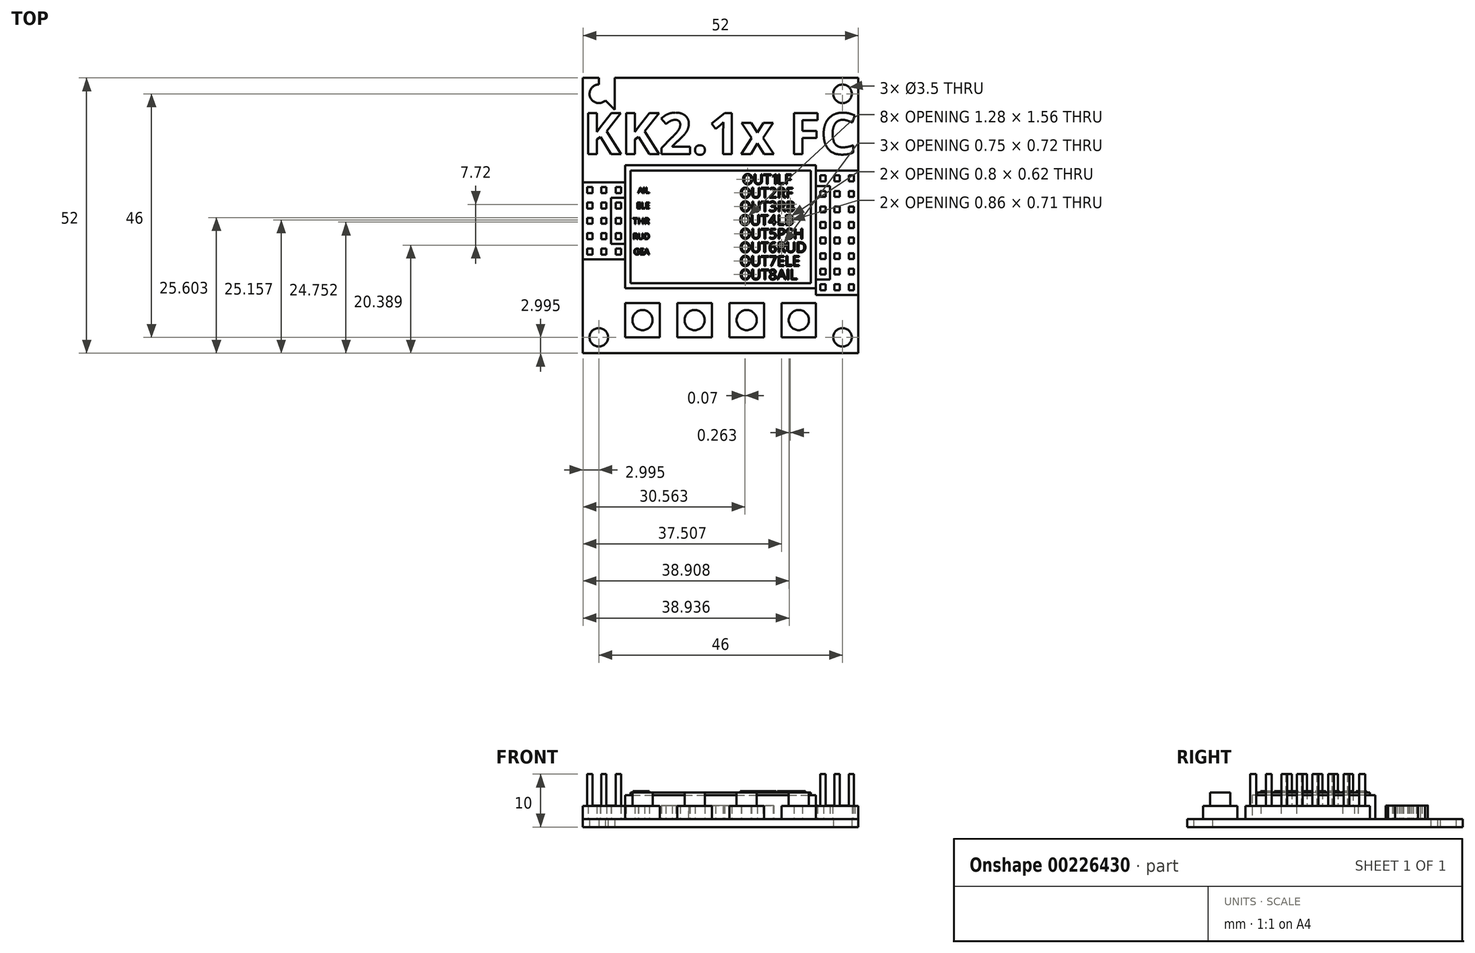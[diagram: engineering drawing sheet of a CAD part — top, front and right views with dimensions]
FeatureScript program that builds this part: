
annotation { "Feature Type Name" : "Feature", "Feature Type Description" : "" }
export const myFeature = defineFeature(function(context is Context, id is Id, definition is map)
    precondition{}
    {
        {
            var Q0;
            Q0=qCreatedBy(makeId("Top.planeOp"),FACE);
            var sketch = newSketch(context, id + "F0", { "sketchPlane" : qUnion([Q0])});
            skLineSegment(sketch, "E0.bottom", {"start": v(-23.53, 22.59) * mm, "end": v(28.47, 22.59) * mm});
            skLineSegment(sketch, "E0.top", {"start": v(-23.53, -29.41) * mm, "end": v(28.47, -29.41) * mm});
            skLineSegment(sketch, "E0.left", {"start": v(-23.53, 22.59) * mm, "end": v(-23.53, -29.41) * mm});
            skLineSegment(sketch, "E0.right", {"start": v(28.47, 22.59) * mm, "end": v(28.47, -29.41) * mm});
            skLineSegment(sketch, "E1", {"start": v(-23.53, 16.59) * mm, "end": v(28.47, 16.59) * mm});
            skLineSegment(sketch, "E2", {"start": v(28.47, -23.41) * mm, "end": v(-23.53, -23.41) * mm});
            skLineSegment(sketch, "E3", {"start": v(-17.53, -29.41) * mm, "end": v(-17.53, 22.59) * mm});
            skLineSegment(sketch, "E4", {"start": v(22.47, 22.59) * mm, "end": v(22.47, -29.41) * mm});
            skLineSegment(sketch, "E5", {"start": v(-23.53, 22.59) * mm, "end": v(-17.53, 16.59) * mm});
            skLineSegment(sketch, "E6", {"start": v(-17.53, 22.59) * mm, "end": v(-23.53, 16.59) * mm});
            skLineSegment(sketch, "E7", {"start": v(-17.53, -23.41) * mm, "end": v(-23.53, -29.41) * mm});
            skLineSegment(sketch, "E8", {"start": v(-23.53, -23.41) * mm, "end": v(-17.53, -29.41) * mm});
            skLineSegment(sketch, "E9", {"start": v(22.47, -29.41) * mm, "end": v(28.47, -23.41) * mm});
            skLineSegment(sketch, "E10", {"start": v(28.47, -29.41) * mm, "end": v(22.47, -23.41) * mm});
            skLineSegment(sketch, "E11", {"start": v(22.47, 16.59) * mm, "end": v(28.47, 22.59) * mm});
            skLineSegment(sketch, "E12", {"start": v(22.47, 22.59) * mm, "end": v(28.47, 16.59) * mm});
            skLineSegment(sketch, "E13", {"start": v(-20.53, 19.59) * mm, "end": v(-23.53, 19.59) * mm});
            skCircle(sketch, "E14", {"center": v(-20.53, 19.59) * mm, "radius": 1.75 * mm});
            skCircle(sketch, "E15", {"center": v(25.47, 19.59) * mm, "radius": 1.75 * mm});
            skCircle(sketch, "E16", {"center": v(25.47, -26.41) * mm, "radius": 1.75 * mm});
            skCircle(sketch, "E17", {"center": v(-20.53, -26.41) * mm, "radius": 1.75 * mm});
            skLineSegment(sketch, "E18", {"start": v(-20.53, 19.59) * mm, "end": v(-20.53, 22.59) * mm});
            skSolve(sketch);
        }
        {
            var Q0;
            {var subQ0=sQuery(id+"F0.wireOp",EDGE,"E1");var subQ1=sQuery(id+"F0.wireOp",EDGE,"E0.right");var subQ2=makeQuery(id+"F0.imprint","INTERSECT",VERTEX,{"derivedFrom":[subQ1,subQ0,sQuery(id+"F0.wireOp",EDGE,"E12")]});Q0=makeQuery(id+"F0.imprint","IMPRINT",FACE,{"disambiguationData":[TD([[makeQuery(id+"F0.imprint","IMPRINT",EDGE,{"disambiguationData":[TD([[subQ2,-1.0]])],"derivedFrom":subQ1}),-1.0]])]});}
            var Q1;
            {var subQ0=sQuery(id+"F0.wireOp",EDGE,"E3");var subQ1=sQuery(id+"F0.wireOp",EDGE,"E1");var subQ2=makeQuery(id+"F0.imprint","INTERSECT",VERTEX,{"derivedFrom":[subQ1,subQ0,sQuery(id+"F0.wireOp",EDGE,"E5")]});Q1=makeQuery(id+"F0.imprint","IMPRINT",FACE,{"disambiguationData":[TD([[makeQuery(id+"F0.imprint","IMPRINT",EDGE,{"disambiguationData":[TD([[subQ2,-1.0]])],"derivedFrom":subQ1}),-1.0]])]});}
            var Q2;
            {var subQ0=sQuery(id+"F0.wireOp",EDGE,"E3");var subQ1=sQuery(id+"F0.wireOp",EDGE,"E0.top");var subQ2=makeQuery(id+"F0.imprint","INTERSECT",VERTEX,{"derivedFrom":[subQ1,subQ0,sQuery(id+"F0.wireOp",EDGE,"E8")]});Q2=makeQuery(id+"F0.imprint","IMPRINT",FACE,{"disambiguationData":[TD([[makeQuery(id+"F0.imprint","IMPRINT",EDGE,{"disambiguationData":[TD([[subQ2,-1.0]])],"derivedFrom":subQ1}),1.0]])]});}
            var Q3;
            {var subQ0=sQuery(id+"F0.wireOp",EDGE,"E1");var subQ1=sQuery(id+"F0.wireOp",EDGE,"E0.left");var subQ2=makeQuery(id+"F0.imprint","INTERSECT",VERTEX,{"derivedFrom":[subQ1,subQ0,sQuery(id+"F0.wireOp",EDGE,"E6")]});Q3=makeQuery(id+"F0.imprint","IMPRINT",FACE,{"disambiguationData":[TD([[makeQuery(id+"F0.imprint","IMPRINT",EDGE,{"disambiguationData":[TD([[subQ2,-1.0]])],"derivedFrom":subQ1}),1.0]])]});}
            var Q4;
            {var subQ0=sQuery(id+"F0.wireOp",EDGE,"E3");var subQ1=sQuery(id+"F0.wireOp",EDGE,"E0.bottom");var subQ2=makeQuery(id+"F0.imprint","INTERSECT",VERTEX,{"derivedFrom":[subQ1,subQ0,sQuery(id+"F0.wireOp",EDGE,"E6")]});Q4=makeQuery(id+"F0.imprint","IMPRINT",FACE,{"disambiguationData":[TD([[makeQuery(id+"F0.imprint","IMPRINT",EDGE,{"disambiguationData":[TD([[subQ2,-1.0]])],"derivedFrom":subQ1}),-1.0]])]});}
            var Q5;
            {var subQ3=sQuery(id+"F0.wireOp",EDGE,"E11");var subQ5=sQuery(id+"F0.wireOp",EDGE,"E15");var subQ6=makeQuery(id+"F0.imprint","INTERSECT",VERTEX,{"disambiguationData":[OD(0.0)],"derivedFrom":[subQ3,subQ5]});Q5=makeQuery(id+"F0.imprint","IMPRINT",FACE,{"disambiguationData":[TD([[makeQuery(id+"F0.imprint","IMPRINT",EDGE,{"disambiguationData":[TD([[subQ6,-1.0]])],"derivedFrom":subQ5}),-1.0]])]});}
            var Q6;
            {var subQ0=sQuery(id+"F0.wireOp",EDGE,"E11");var subQ5=sQuery(id+"F0.wireOp",EDGE,"E15");var subQ6=makeQuery(id+"F0.imprint","INTERSECT",VERTEX,{"disambiguationData":[OD(1.0)],"derivedFrom":[subQ0,subQ5]});Q6=makeQuery(id+"F0.imprint","IMPRINT",FACE,{"disambiguationData":[TD([[makeQuery(id+"F0.imprint","IMPRINT",EDGE,{"disambiguationData":[TD([[subQ6,1.0]])],"derivedFrom":subQ5}),-1.0]])]});}
            var Q7;
            {var subQ0=sQuery(id+"F0.wireOp",EDGE,"E11");var subQ5=sQuery(id+"F0.wireOp",EDGE,"E15");var subQ6=makeQuery(id+"F0.imprint","INTERSECT",VERTEX,{"disambiguationData":[OD(1.0)],"derivedFrom":[subQ0,subQ5]});Q7=makeQuery(id+"F0.imprint","IMPRINT",FACE,{"disambiguationData":[TD([[makeQuery(id+"F0.imprint","IMPRINT",EDGE,{"disambiguationData":[TD([[subQ6,-1.0]])],"derivedFrom":subQ5}),-1.0]])]});}
            var Q8;
            {var subQ3=sQuery(id+"F0.wireOp",EDGE,"E11");var subQ5=sQuery(id+"F0.wireOp",EDGE,"E15");var subQ6=makeQuery(id+"F0.imprint","INTERSECT",VERTEX,{"disambiguationData":[OD(0.0)],"derivedFrom":[subQ3,subQ5]});Q8=makeQuery(id+"F0.imprint","IMPRINT",FACE,{"disambiguationData":[TD([[makeQuery(id+"F0.imprint","IMPRINT",EDGE,{"disambiguationData":[TD([[subQ6,1.0]])],"derivedFrom":subQ5}),-1.0]])]});}
            var Q9;
            {var subQ3=sQuery(id+"F0.wireOp",EDGE,"E9");var subQ5=sQuery(id+"F0.wireOp",EDGE,"E16");var subQ6=makeQuery(id+"F0.imprint","INTERSECT",VERTEX,{"disambiguationData":[OD(1.0)],"derivedFrom":[subQ3,subQ5]});Q9=makeQuery(id+"F0.imprint","IMPRINT",FACE,{"disambiguationData":[TD([[makeQuery(id+"F0.imprint","IMPRINT",EDGE,{"disambiguationData":[TD([[subQ6,1.0]])],"derivedFrom":subQ5}),-1.0]])]});}
            var Q10;
            {var subQ0=sQuery(id+"F0.wireOp",EDGE,"E9");var subQ5=sQuery(id+"F0.wireOp",EDGE,"E16");var subQ6=makeQuery(id+"F0.imprint","INTERSECT",VERTEX,{"disambiguationData":[OD(1.0)],"derivedFrom":[subQ0,subQ5]});Q10=makeQuery(id+"F0.imprint","IMPRINT",FACE,{"disambiguationData":[TD([[makeQuery(id+"F0.imprint","IMPRINT",EDGE,{"disambiguationData":[TD([[subQ6,-1.0]])],"derivedFrom":subQ5}),-1.0]])]});}
            var Q11;
            {var subQ0=sQuery(id+"F0.wireOp",EDGE,"E9");var subQ5=sQuery(id+"F0.wireOp",EDGE,"E16");var subQ6=makeQuery(id+"F0.imprint","INTERSECT",VERTEX,{"disambiguationData":[OD(0.0)],"derivedFrom":[subQ0,subQ5]});Q11=makeQuery(id+"F0.imprint","IMPRINT",FACE,{"disambiguationData":[TD([[makeQuery(id+"F0.imprint","IMPRINT",EDGE,{"disambiguationData":[TD([[subQ6,1.0]])],"derivedFrom":subQ5}),-1.0]])]});}
            var Q12;
            {var subQ3=sQuery(id+"F0.wireOp",EDGE,"E9");var subQ5=sQuery(id+"F0.wireOp",EDGE,"E16");var subQ7=makeQuery(id+"F0.imprint","INTERSECT",VERTEX,{"disambiguationData":[OD(0.0)],"derivedFrom":[subQ3,subQ5]});Q12=makeQuery(id+"F0.imprint","IMPRINT",FACE,{"disambiguationData":[TD([[makeQuery(id+"F0.imprint","IMPRINT",EDGE,{"disambiguationData":[TD([[subQ7,-1.0]])],"derivedFrom":subQ5}),-1.0]])]});}
            var Q13;
            {var subQ0=sQuery(id+"F0.wireOp",EDGE,"E7");var subQ5=sQuery(id+"F0.wireOp",EDGE,"E17");var subQ6=makeQuery(id+"F0.imprint","INTERSECT",VERTEX,{"disambiguationData":[OD(1.0)],"derivedFrom":[subQ0,subQ5]});Q13=makeQuery(id+"F0.imprint","IMPRINT",FACE,{"disambiguationData":[TD([[makeQuery(id+"F0.imprint","IMPRINT",EDGE,{"disambiguationData":[TD([[subQ6,-1.0]])],"derivedFrom":subQ5}),-1.0]])]});}
            var Q14;
            {var subQ3=sQuery(id+"F0.wireOp",EDGE,"E7");var subQ5=sQuery(id+"F0.wireOp",EDGE,"E17");var subQ6=makeQuery(id+"F0.imprint","INTERSECT",VERTEX,{"disambiguationData":[OD(0.0)],"derivedFrom":[subQ3,subQ5]});Q14=makeQuery(id+"F0.imprint","IMPRINT",FACE,{"disambiguationData":[TD([[makeQuery(id+"F0.imprint","IMPRINT",EDGE,{"disambiguationData":[TD([[subQ6,1.0]])],"derivedFrom":subQ5}),-1.0]])]});}
            var Q15;
            {var subQ3=sQuery(id+"F0.wireOp",EDGE,"E7");var subQ5=sQuery(id+"F0.wireOp",EDGE,"E17");var subQ6=makeQuery(id+"F0.imprint","INTERSECT",VERTEX,{"disambiguationData":[OD(0.0)],"derivedFrom":[subQ3,subQ5]});Q15=makeQuery(id+"F0.imprint","IMPRINT",FACE,{"disambiguationData":[TD([[makeQuery(id+"F0.imprint","IMPRINT",EDGE,{"disambiguationData":[TD([[subQ6,-1.0]])],"derivedFrom":subQ5}),-1.0]])]});}
            var Q16;
            {var subQ0=sQuery(id+"F0.wireOp",EDGE,"E7");var subQ5=sQuery(id+"F0.wireOp",EDGE,"E17");var subQ6=makeQuery(id+"F0.imprint","INTERSECT",VERTEX,{"disambiguationData":[OD(1.0)],"derivedFrom":[subQ0,subQ5]});Q16=makeQuery(id+"F0.imprint","IMPRINT",FACE,{"disambiguationData":[TD([[makeQuery(id+"F0.imprint","IMPRINT",EDGE,{"disambiguationData":[TD([[subQ6,1.0]])],"derivedFrom":subQ5}),-1.0]])]});}
            var Q17;
            {var subQ1=sQuery(id+"F0.wireOp",EDGE,"E0.left");var subQ3=sQuery(id+"F0.wireOp",EDGE,"E13");var subQ4=makeQuery(id+"F0.imprint","INTERSECT",VERTEX,{"derivedFrom":[subQ1,subQ3]});Q17=makeQuery(id+"F0.imprint","IMPRINT",FACE,{"disambiguationData":[TD([[makeQuery(id+"F0.imprint","IMPRINT",EDGE,{"disambiguationData":[TD([[subQ4,1.0]])],"derivedFrom":subQ3}),-1.0]])]});}
            var Q18;
            {var subQ0=sQuery(id+"F0.wireOp",EDGE,"E5");var subQ5=sQuery(id+"F0.wireOp",EDGE,"E14");var subQ6=makeQuery(id+"F0.imprint","INTERSECT",VERTEX,{"disambiguationData":[OD(0.0)],"derivedFrom":[subQ0,subQ5]});Q18=makeQuery(id+"F0.imprint","IMPRINT",FACE,{"disambiguationData":[TD([[makeQuery(id+"F0.imprint","IMPRINT",EDGE,{"disambiguationData":[TD([[subQ6,1.0]])],"derivedFrom":subQ5}),-1.0]])]});}
            var Q19;
            {var subQ0=sQuery(id+"F0.wireOp",EDGE,"E6");var subQ5=sQuery(id+"F0.wireOp",EDGE,"E14");var subQ6=makeQuery(id+"F0.imprint","INTERSECT",VERTEX,{"disambiguationData":[OD(0.0)],"derivedFrom":[subQ0,subQ5]});Q19=makeQuery(id+"F0.imprint","IMPRINT",FACE,{"disambiguationData":[TD([[makeQuery(id+"F0.imprint","IMPRINT",EDGE,{"disambiguationData":[TD([[subQ6,-1.0]])],"derivedFrom":subQ5}),-1.0]])]});}
            var Q20;
            {var subQ3=sQuery(id+"F0.wireOp",EDGE,"E5");var subQ5=sQuery(id+"F0.wireOp",EDGE,"E14");var subQ6=makeQuery(id+"F0.imprint","INTERSECT",VERTEX,{"disambiguationData":[OD(1.0)],"derivedFrom":[subQ3,subQ5]});Q20=makeQuery(id+"F0.imprint","IMPRINT",FACE,{"disambiguationData":[TD([[makeQuery(id+"F0.imprint","IMPRINT",EDGE,{"disambiguationData":[TD([[subQ6,-1.0]])],"derivedFrom":subQ5}),-1.0]])]});}
            var Q21;
            {var subQ3=sQuery(id+"F0.wireOp",EDGE,"E5");var subQ5=sQuery(id+"F0.wireOp",EDGE,"E14");var subQ6=makeQuery(id+"F0.imprint","INTERSECT",VERTEX,{"disambiguationData":[OD(1.0)],"derivedFrom":[subQ3,subQ5]});Q21=makeQuery(id+"F0.imprint","IMPRINT",FACE,{"disambiguationData":[TD([[makeQuery(id+"F0.imprint","IMPRINT",EDGE,{"disambiguationData":[TD([[subQ6,1.0]])],"derivedFrom":subQ5}),-1.0]])]});}
            var Q22;
            {var subQ1=sQuery(id+"F0.wireOp",EDGE,"E0.left");var subQ3=sQuery(id+"F0.wireOp",EDGE,"E13");var subQ4=makeQuery(id+"F0.imprint","INTERSECT",VERTEX,{"derivedFrom":[subQ1,subQ3]});Q22=makeQuery(id+"F0.imprint","IMPRINT",FACE,{"disambiguationData":[TD([[makeQuery(id+"F0.imprint","IMPRINT",EDGE,{"disambiguationData":[TD([[subQ4,1.0]])],"derivedFrom":subQ3}),1.0]])]});}
            extrude(context, id + "F1", {"entities" : qUnion([Q0, Q1, Q2, Q3, Q4, Q5, Q6, Q7, Q8, Q9, Q10, Q11, Q12, Q13, Q14, Q15, Q16, Q17, Q18, Q19, Q20, Q21, Q22]), "depth" : 1.5 * mm, "offsetDistance" : 25.4 * mm});
        }
        {
            var Q0;
            Q0=makeQuery(id+"F1.opExtrude","CAP_FACE",FACE,{"disambiguationData":[OSD([sQuery(id+"F0.wireOp",EDGE,"E0.bottom"),sQuery(id+"F0.wireOp",EDGE,"E0.top"),sQuery(id+"F0.wireOp",EDGE,"E0.left"),sQuery(id+"F0.wireOp",EDGE,"E0.right"),sQuery(id+"F0.wireOp",EDGE,"E14"),sQuery(id+"F0.wireOp",EDGE,"E15"),sQuery(id+"F0.wireOp",EDGE,"E16"),sQuery(id+"F0.wireOp",EDGE,"E17")])],"isStart":false});
            var sketch = newSketch(context, id + "F2", { "sketchPlane" : qUnion([Q0])});
            skLineSegment(sketch, "E19.bottom", {"start": v(-15.53, 6.09) * mm, "end": v(20.47, 6.09) * mm});
            skLineSegment(sketch, "E19.top", {"start": v(-15.53, -17.16) * mm, "end": v(20.47, -17.16) * mm});
            skLineSegment(sketch, "E19.left", {"start": v(-15.53, 6.09) * mm, "end": v(-15.53, -17.16) * mm});
            skLineSegment(sketch, "E19.right", {"start": v(20.47, 6.09) * mm, "end": v(20.47, -17.16) * mm});
            skLineSegment(sketch, "E20", {"start": v(-15.53, 6.09) * mm, "end": v(-23.53, 6.09) * mm});
            skLineSegment(sketch, "E21", {"start": v(20.47, 6.09) * mm, "end": v(28.47, 6.09) * mm});
            skSolve(sketch);
        }
        {
            var Q0;
            Q0=makeQuery(id+"F2.imprint","IMPRINT",FACE,{"disambiguationData":[TD([[makeQuery(id+"F2.imprint","IMPRINT",EDGE,{"derivedFrom":sQuery(id+"F2.wireOp",EDGE,"E19.bottom")}),-1.0]])]});
            extrude(context, id + "F3", {"entities" : qUnion([Q0]), "depth" : 4.5 * mm, "offsetDistance" : 25.4 * mm});
        }
        {
            var Q0;
            Q0=makeQuery(id+"F3.opExtrude","CAP_FACE",FACE,{"disambiguationData":[OSD([sQuery(id+"F2.wireOp",EDGE,"E19.bottom"),sQuery(id+"F2.wireOp",EDGE,"E19.top"),sQuery(id+"F2.wireOp",EDGE,"E19.left"),sQuery(id+"F2.wireOp",EDGE,"E19.right")])],"isStart":false});
            var sketch = newSketch(context, id + "F4", { "sketchPlane" : qUnion([Q0])});
            skLineSegment(sketch, "E22.bottom", {"start": v(-14.53, 5.09) * mm, "end": v(19.47, 5.09) * mm});
            skLineSegment(sketch, "E22.top", {"start": v(-14.53, -16.16) * mm, "end": v(19.47, -16.16) * mm});
            skLineSegment(sketch, "E22.left", {"start": v(-14.53, 5.09) * mm, "end": v(-14.53, -16.16) * mm});
            skLineSegment(sketch, "E22.right", {"start": v(19.47, 5.09) * mm, "end": v(19.47, -16.16) * mm});
            skLineSegment(sketch, "E23", {"start": v(-14.53, 5.09) * mm, "end": v(-14.53, 6.09) * mm});
            skLineSegment(sketch, "E24", {"start": v(-14.53, -16.16) * mm, "end": v(-14.53, -17.16) * mm});
            skLineSegment(sketch, "E25", {"start": v(19.47, 5.09) * mm, "end": v(20.47, 5.09) * mm});
            skLineSegment(sketch, "E26", {"start": v(-14.53, 5.09) * mm, "end": v(-15.53, 5.09) * mm});
            skSolve(sketch);
        }
        {
            var Q0;
            Q0=makeQuery(id+"F4.imprint","IMPRINT",FACE,{"disambiguationData":[TD([[makeQuery(id+"F4.imprint","IMPRINT",EDGE,{"derivedFrom":sQuery(id+"F4.wireOp",EDGE,"E22.bottom")}),-1.0]])]});
            extrude(context, id + "F5", {"entities" : qUnion([Q0]), "depth" : 0.5 * mm, "offsetDistance" : 25.4 * mm});
        }
        {
            var Q0;
            Q0=makeQuery(id+"F1.opExtrude","CAP_FACE",FACE,{"disambiguationData":[OSD([sQuery(id+"F0.wireOp",EDGE,"E0.bottom"),sQuery(id+"F0.wireOp",EDGE,"E0.top"),sQuery(id+"F0.wireOp",EDGE,"E0.left"),sQuery(id+"F0.wireOp",EDGE,"E0.right"),sQuery(id+"F0.wireOp",EDGE,"E14"),sQuery(id+"F0.wireOp",EDGE,"E15"),sQuery(id+"F0.wireOp",EDGE,"E16"),sQuery(id+"F0.wireOp",EDGE,"E17")])],"isStart":false});
            var sketch = newSketch(context, id + "F6", { "sketchPlane" : qUnion([Q0])});
            skLineSegment(sketch, "E27.0", {"start": v(-15.53, 6.09) * mm, "end": v(-15.53, -17.16) * mm});
            skLineSegment(sketch, "E27.1", {"start": v(-15.53, -17.16) * mm, "end": v(20.47, -17.16) * mm});
            skLineSegment(sketch, "E27.2", {"start": v(20.47, 6.09) * mm, "end": v(20.47, -17.16) * mm});
            skLineSegment(sketch, "E27.3", {"start": v(-15.53, 6.09) * mm, "end": v(20.47, 6.09) * mm});
            skLineSegment(sketch, "E28.bottom", {"start": v(-23.53, 2.84) * mm, "end": v(-15.53, 2.84) * mm});
            skLineSegment(sketch, "E28.top", {"start": v(-23.53, -11.66) * mm, "end": v(-15.53, -11.66) * mm});
            skLineSegment(sketch, "E28.left", {"start": v(-23.53, 2.84) * mm, "end": v(-23.53, -11.66) * mm});
            skLineSegment(sketch, "E28.right", {"start": v(-15.53, 2.84) * mm, "end": v(-15.53, -11.66) * mm});
            skLineSegment(sketch, "E29.bottom", {"start": v(28.47, 5.09) * mm, "end": v(20.47, 5.09) * mm});
            skLineSegment(sketch, "E29.top", {"start": v(28.47, -18.41) * mm, "end": v(20.47, -18.41) * mm});
            skLineSegment(sketch, "E29.left", {"start": v(28.47, 5.09) * mm, "end": v(28.47, -18.41) * mm});
            skLineSegment(sketch, "E29.right", {"start": v(20.47, 5.09) * mm, "end": v(20.47, -18.41) * mm});
            skLineSegment(sketch, "E30", {"start": v(-23.53, -0.06) * mm, "end": v(-15.53, -0.06) * mm});
            skLineSegment(sketch, "E31", {"start": v(-23.53, -2.96) * mm, "end": v(-15.53, -2.96) * mm});
            skLineSegment(sketch, "E32", {"start": v(-23.53, -5.86) * mm, "end": v(-15.53, -5.86) * mm});
            skLineSegment(sketch, "E33", {"start": v(-23.53, -8.76) * mm, "end": v(-15.53, -8.76) * mm});
            skLineSegment(sketch, "E34", {"start": v(-20.91, 2.84) * mm, "end": v(-20.91, -11.66) * mm});
            skLineSegment(sketch, "E35", {"start": v(-18.22, -11.66) * mm, "end": v(-18.22, 2.84) * mm});
            skLineSegment(sketch, "E36", {"start": v(-18.22, 0) * mm, "end": v(-15.53, 2.84) * mm, "construction": true});
            skLineSegment(sketch, "E37", {"start": v(-20.91, 0) * mm, "end": v(-18.22, 2.84) * mm, "construction": true});
            skLineSegment(sketch, "E38", {"start": v(-23.53, -0.06) * mm, "end": v(-20.91, 2.84) * mm, "construction": true});
            skLineSegment(sketch, "E39", {"start": v(-23.53, -0.06) * mm, "end": v(-20.91, -2.96) * mm, "construction": true});
            skLineSegment(sketch, "E40", {"start": v(-20.91, -2.96) * mm, "end": v(-23.53, -5.86) * mm, "construction": true});
            skLineSegment(sketch, "E41", {"start": v(-20.91, -8.76) * mm, "end": v(-23.53, -5.86) * mm, "construction": true});
            skLineSegment(sketch, "E42", {"start": v(-20.91, -8.76) * mm, "end": v(-23.53, -11.66) * mm, "construction": true});
            skLineSegment(sketch, "E43", {"start": v(20.47, -0.79) * mm, "end": v(28.47, -0.79) * mm});
            skLineSegment(sketch, "E44", {"start": v(20.47, -3.73) * mm, "end": v(28.47, -3.73) * mm});
            skLineSegment(sketch, "E45", {"start": v(20.47, -6.66) * mm, "end": v(28.47, -6.66) * mm});
            skLineSegment(sketch, "E46", {"start": v(20.47, -9.6) * mm, "end": v(28.47, -9.6) * mm});
            skLineSegment(sketch, "E47", {"start": v(20.47, -12.54) * mm, "end": v(28.47, -12.54) * mm});
            skLineSegment(sketch, "E48", {"start": v(20.47, -15.48) * mm, "end": v(28.47, -15.48) * mm});
            skLineSegment(sketch, "E49", {"start": v(20.47, 2.15) * mm, "end": v(28.47, 2.15) * mm});
            skLineSegment(sketch, "E50", {"start": v(23.13, 5.09) * mm, "end": v(23.13, -18.41) * mm});
            skLineSegment(sketch, "E51", {"start": v(25.8, -18.41) * mm, "end": v(25.8, 5.09) * mm});
            skLineSegment(sketch, "E52", {"start": v(20.47, 5.09) * mm, "end": v(23.13, 2.15) * mm, "construction": true});
            skLineSegment(sketch, "E53", {"start": v(23.13, 2.15) * mm, "end": v(25.8, 5.09) * mm, "construction": true});
            skLineSegment(sketch, "E54", {"start": v(25.8, 5.09) * mm, "end": v(28.47, 2.15) * mm, "construction": true});
            skLineSegment(sketch, "E55", {"start": v(23.13, 2.15) * mm, "end": v(20.47, -0.79) * mm, "construction": true});
            skLineSegment(sketch, "E56", {"start": v(20.47, -0.79) * mm, "end": v(23.13, -3.73) * mm, "construction": true});
            skLineSegment(sketch, "E57", {"start": v(23.13, -3.73) * mm, "end": v(20.47, -6.66) * mm, "construction": true});
            skLineSegment(sketch, "E58", {"start": v(20.47, -6.66) * mm, "end": v(23.13, -9.6) * mm, "construction": true});
            skLineSegment(sketch, "E59", {"start": v(23.13, -9.6) * mm, "end": v(20.47, -12.54) * mm, "construction": true});
            skLineSegment(sketch, "E60", {"start": v(20.47, -12.54) * mm, "end": v(23.13, -15.48) * mm, "construction": true});
            skLineSegment(sketch, "E61", {"start": v(23.13, -15.48) * mm, "end": v(20.47, -18.41) * mm, "construction": true});
            skSolve(sketch);
        }
        {
            var Q0;
            {var subQ0=sQuery(id+"F6.wireOp",EDGE,"E28.left");var subQ5=sQuery(id+"F6.wireOp",EDGE,"E30");var subQ6=makeQuery(id+"F6.imprint","INTERSECT",VERTEX,{"derivedFrom":[subQ0,subQ5]});Q0=makeQuery(id+"F6.imprint","IMPRINT",FACE,{"disambiguationData":[TD([[makeQuery(id+"F6.imprint","IMPRINT",EDGE,{"disambiguationData":[TD([[subQ6,-1.0]])],"derivedFrom":subQ5}),1.0]])]});}
            var Q1;
            {var subQ0=sQuery(id+"F6.wireOp",EDGE,"E34");var subQ1=sQuery(id+"F6.wireOp",EDGE,"E28.bottom");var subQ2=makeQuery(id+"F6.imprint","INTERSECT",VERTEX,{"derivedFrom":[subQ1,subQ0]});Q1=makeQuery(id+"F6.imprint","IMPRINT",FACE,{"disambiguationData":[TD([[makeQuery(id+"F6.imprint","IMPRINT",EDGE,{"disambiguationData":[TD([[subQ2,-1.0]])],"derivedFrom":subQ1}),-1.0]])]});}
            var Q2;
            {var subQ0=sQuery(id+"F6.wireOp",EDGE,"E28.right");var subQ5=sQuery(id+"F6.wireOp",EDGE,"E30");var subQ7=makeQuery(id+"F6.imprint","INTERSECT",VERTEX,{"derivedFrom":[subQ0,subQ5]});Q2=makeQuery(id+"F6.imprint","IMPRINT",FACE,{"disambiguationData":[TD([[makeQuery(id+"F6.imprint","IMPRINT",EDGE,{"disambiguationData":[TD([[subQ7,1.0]])],"derivedFrom":subQ5}),1.0]])]});}
            var Q3;
            {var subQ0=sQuery(id+"F6.wireOp",EDGE,"E30");var subQ1=sQuery(id+"F6.wireOp",EDGE,"E28.right");var subQ2=makeQuery(id+"F6.imprint","INTERSECT",VERTEX,{"derivedFrom":[subQ1,subQ0]});Q3=makeQuery(id+"F6.imprint","IMPRINT",FACE,{"disambiguationData":[TD([[makeQuery(id+"F6.imprint","IMPRINT",EDGE,{"disambiguationData":[TD([[subQ2,-1.0]])],"derivedFrom":subQ1}),-1.0]])]});}
            var Q4;
            {var subQ0=sQuery(id+"F6.wireOp",EDGE,"E34");var subQ1=sQuery(id+"F6.wireOp",EDGE,"E30");var subQ2=makeQuery(id+"F6.imprint","INTERSECT",VERTEX,{"derivedFrom":[subQ1,subQ0]});Q4=makeQuery(id+"F6.imprint","IMPRINT",FACE,{"disambiguationData":[TD([[makeQuery(id+"F6.imprint","IMPRINT",EDGE,{"disambiguationData":[TD([[subQ2,-1.0]])],"derivedFrom":subQ1}),-1.0]])]});}
            var Q5;
            {var subQ0=sQuery(id+"F6.wireOp",EDGE,"E30");var subQ1=sQuery(id+"F6.wireOp",EDGE,"E28.left");var subQ2=makeQuery(id+"F6.imprint","INTERSECT",VERTEX,{"derivedFrom":[subQ1,subQ0]});Q5=makeQuery(id+"F6.imprint","IMPRINT",FACE,{"disambiguationData":[TD([[makeQuery(id+"F6.imprint","IMPRINT",EDGE,{"disambiguationData":[TD([[subQ2,-1.0]])],"derivedFrom":subQ1}),1.0]])]});}
            var Q6;
            {var subQ0=sQuery(id+"F6.wireOp",EDGE,"E31");var subQ1=sQuery(id+"F6.wireOp",EDGE,"E28.left");var subQ2=makeQuery(id+"F6.imprint","INTERSECT",VERTEX,{"derivedFrom":[subQ1,subQ0]});Q6=makeQuery(id+"F6.imprint","IMPRINT",FACE,{"disambiguationData":[TD([[makeQuery(id+"F6.imprint","IMPRINT",EDGE,{"disambiguationData":[TD([[subQ2,-1.0]])],"derivedFrom":subQ1}),1.0]])]});}
            var Q7;
            {var subQ0=sQuery(id+"F6.wireOp",EDGE,"E34");var subQ1=sQuery(id+"F6.wireOp",EDGE,"E31");var subQ2=makeQuery(id+"F6.imprint","INTERSECT",VERTEX,{"derivedFrom":[subQ1,subQ0]});Q7=makeQuery(id+"F6.imprint","IMPRINT",FACE,{"disambiguationData":[TD([[makeQuery(id+"F6.imprint","IMPRINT",EDGE,{"disambiguationData":[TD([[subQ2,-1.0]])],"derivedFrom":subQ1}),-1.0]])]});}
            var Q8;
            {var subQ0=sQuery(id+"F6.wireOp",EDGE,"E31");var subQ1=sQuery(id+"F6.wireOp",EDGE,"E28.right");var subQ2=makeQuery(id+"F6.imprint","INTERSECT",VERTEX,{"derivedFrom":[subQ1,subQ0]});Q8=makeQuery(id+"F6.imprint","IMPRINT",FACE,{"disambiguationData":[TD([[makeQuery(id+"F6.imprint","IMPRINT",EDGE,{"disambiguationData":[TD([[subQ2,-1.0]])],"derivedFrom":subQ1}),-1.0]])]});}
            var Q9;
            {var subQ0=sQuery(id+"F6.wireOp",EDGE,"E32");var subQ1=sQuery(id+"F6.wireOp",EDGE,"E28.right");var subQ2=makeQuery(id+"F6.imprint","INTERSECT",VERTEX,{"derivedFrom":[subQ1,subQ0]});Q9=makeQuery(id+"F6.imprint","IMPRINT",FACE,{"disambiguationData":[TD([[makeQuery(id+"F6.imprint","IMPRINT",EDGE,{"disambiguationData":[TD([[subQ2,-1.0]])],"derivedFrom":subQ1}),-1.0]])]});}
            var Q10;
            {var subQ0=sQuery(id+"F6.wireOp",EDGE,"E34");var subQ1=sQuery(id+"F6.wireOp",EDGE,"E32");var subQ2=makeQuery(id+"F6.imprint","INTERSECT",VERTEX,{"derivedFrom":[subQ1,subQ0]});Q10=makeQuery(id+"F6.imprint","IMPRINT",FACE,{"disambiguationData":[TD([[makeQuery(id+"F6.imprint","IMPRINT",EDGE,{"disambiguationData":[TD([[subQ2,-1.0]])],"derivedFrom":subQ1}),-1.0]])]});}
            var Q11;
            {var subQ0=sQuery(id+"F6.wireOp",EDGE,"E32");var subQ1=sQuery(id+"F6.wireOp",EDGE,"E28.left");var subQ2=makeQuery(id+"F6.imprint","INTERSECT",VERTEX,{"derivedFrom":[subQ1,subQ0]});Q11=makeQuery(id+"F6.imprint","IMPRINT",FACE,{"disambiguationData":[TD([[makeQuery(id+"F6.imprint","IMPRINT",EDGE,{"disambiguationData":[TD([[subQ2,-1.0]])],"derivedFrom":subQ1}),1.0]])]});}
            var Q12;
            {var subQ0=sQuery(id+"F6.wireOp",EDGE,"E28.left");var subQ5=sQuery(id+"F6.wireOp",EDGE,"E33");var subQ6=makeQuery(id+"F6.imprint","INTERSECT",VERTEX,{"derivedFrom":[subQ0,subQ5]});Q12=makeQuery(id+"F6.imprint","IMPRINT",FACE,{"disambiguationData":[TD([[makeQuery(id+"F6.imprint","IMPRINT",EDGE,{"disambiguationData":[TD([[subQ6,-1.0]])],"derivedFrom":subQ5}),-1.0]])]});}
            var Q13;
            {var subQ0=sQuery(id+"F6.wireOp",EDGE,"E34");var subQ1=sQuery(id+"F6.wireOp",EDGE,"E28.top");var subQ2=makeQuery(id+"F6.imprint","INTERSECT",VERTEX,{"derivedFrom":[subQ1,subQ0]});Q13=makeQuery(id+"F6.imprint","IMPRINT",FACE,{"disambiguationData":[TD([[makeQuery(id+"F6.imprint","IMPRINT",EDGE,{"disambiguationData":[TD([[subQ2,-1.0]])],"derivedFrom":subQ1}),1.0]])]});}
            var Q14;
            {var subQ0=sQuery(id+"F6.wireOp",EDGE,"E28.right");var subQ5=sQuery(id+"F6.wireOp",EDGE,"E33");var subQ6=makeQuery(id+"F6.imprint","INTERSECT",VERTEX,{"derivedFrom":[subQ0,subQ5]});Q14=makeQuery(id+"F6.imprint","IMPRINT",FACE,{"disambiguationData":[TD([[makeQuery(id+"F6.imprint","IMPRINT",EDGE,{"disambiguationData":[TD([[subQ6,1.0]])],"derivedFrom":subQ5}),-1.0]])]});}
            var Q15;
            {var subQ0=sQuery(id+"F6.wireOp",EDGE,"E29.right");var subQ5=sQuery(id+"F6.wireOp",EDGE,"E49");var subQ6=makeQuery(id+"F6.imprint","INTERSECT",VERTEX,{"derivedFrom":[subQ0,subQ5]});Q15=makeQuery(id+"F6.imprint","IMPRINT",FACE,{"disambiguationData":[TD([[makeQuery(id+"F6.imprint","IMPRINT",EDGE,{"disambiguationData":[TD([[subQ6,-1.0]])],"derivedFrom":subQ5}),1.0]])]});}
            var Q16;
            {var subQ0=sQuery(id+"F6.wireOp",EDGE,"E50");var subQ1=sQuery(id+"F6.wireOp",EDGE,"E29.bottom");var subQ2=makeQuery(id+"F6.imprint","INTERSECT",VERTEX,{"derivedFrom":[subQ1,subQ0]});Q16=makeQuery(id+"F6.imprint","IMPRINT",FACE,{"disambiguationData":[TD([[makeQuery(id+"F6.imprint","IMPRINT",EDGE,{"disambiguationData":[TD([[subQ2,1.0]])],"derivedFrom":subQ1}),1.0]])]});}
            var Q17;
            {var subQ0=sQuery(id+"F6.wireOp",EDGE,"E29.left");var subQ5=sQuery(id+"F6.wireOp",EDGE,"E49");var subQ6=makeQuery(id+"F6.imprint","INTERSECT",VERTEX,{"derivedFrom":[subQ0,subQ5]});Q17=makeQuery(id+"F6.imprint","IMPRINT",FACE,{"disambiguationData":[TD([[makeQuery(id+"F6.imprint","IMPRINT",EDGE,{"disambiguationData":[TD([[subQ6,1.0]])],"derivedFrom":subQ5}),1.0]])]});}
            var Q18;
            {var subQ0=sQuery(id+"F6.wireOp",EDGE,"E43");var subQ1=sQuery(id+"F6.wireOp",EDGE,"E29.left");var subQ2=makeQuery(id+"F6.imprint","INTERSECT",VERTEX,{"derivedFrom":[subQ1,subQ0]});Q18=makeQuery(id+"F6.imprint","IMPRINT",FACE,{"disambiguationData":[TD([[makeQuery(id+"F6.imprint","IMPRINT",EDGE,{"disambiguationData":[TD([[subQ2,1.0]])],"derivedFrom":subQ1}),-1.0]])]});}
            var Q19;
            {var subQ0=sQuery(id+"F6.wireOp",EDGE,"E50");var subQ1=sQuery(id+"F6.wireOp",EDGE,"E43");var subQ2=makeQuery(id+"F6.imprint","INTERSECT",VERTEX,{"derivedFrom":[subQ1,subQ0]});Q19=makeQuery(id+"F6.imprint","IMPRINT",FACE,{"disambiguationData":[TD([[makeQuery(id+"F6.imprint","IMPRINT",EDGE,{"disambiguationData":[TD([[subQ2,-1.0]])],"derivedFrom":subQ1}),1.0]])]});}
            var Q20;
            {var subQ0=sQuery(id+"F6.wireOp",EDGE,"E43");var subQ1=sQuery(id+"F6.wireOp",EDGE,"E29.right");var subQ2=makeQuery(id+"F6.imprint","INTERSECT",VERTEX,{"derivedFrom":[subQ1,subQ0]});Q20=makeQuery(id+"F6.imprint","IMPRINT",FACE,{"disambiguationData":[TD([[makeQuery(id+"F6.imprint","IMPRINT",EDGE,{"disambiguationData":[TD([[subQ2,1.0]])],"derivedFrom":subQ1}),1.0]])]});}
            var Q21;
            {var subQ0=sQuery(id+"F6.wireOp",EDGE,"E43");var subQ1=sQuery(id+"F6.wireOp",EDGE,"E29.right");var subQ2=makeQuery(id+"F6.imprint","INTERSECT",VERTEX,{"derivedFrom":[subQ1,subQ0]});Q21=makeQuery(id+"F6.imprint","IMPRINT",FACE,{"disambiguationData":[TD([[makeQuery(id+"F6.imprint","IMPRINT",EDGE,{"disambiguationData":[TD([[subQ2,-1.0]])],"derivedFrom":subQ1}),1.0]])]});}
            var Q22;
            {var subQ0=sQuery(id+"F6.wireOp",EDGE,"E50");var subQ1=sQuery(id+"F6.wireOp",EDGE,"E43");var subQ2=makeQuery(id+"F6.imprint","INTERSECT",VERTEX,{"derivedFrom":[subQ1,subQ0]});Q22=makeQuery(id+"F6.imprint","IMPRINT",FACE,{"disambiguationData":[TD([[makeQuery(id+"F6.imprint","IMPRINT",EDGE,{"disambiguationData":[TD([[subQ2,-1.0]])],"derivedFrom":subQ1}),-1.0]])]});}
            var Q23;
            {var subQ0=sQuery(id+"F6.wireOp",EDGE,"E43");var subQ1=sQuery(id+"F6.wireOp",EDGE,"E29.left");var subQ2=makeQuery(id+"F6.imprint","INTERSECT",VERTEX,{"derivedFrom":[subQ1,subQ0]});Q23=makeQuery(id+"F6.imprint","IMPRINT",FACE,{"disambiguationData":[TD([[makeQuery(id+"F6.imprint","IMPRINT",EDGE,{"disambiguationData":[TD([[subQ2,-1.0]])],"derivedFrom":subQ1}),-1.0]])]});}
            var Q24;
            {var subQ0=sQuery(id+"F6.wireOp",EDGE,"E44");var subQ1=sQuery(id+"F6.wireOp",EDGE,"E29.left");var subQ2=makeQuery(id+"F6.imprint","INTERSECT",VERTEX,{"derivedFrom":[subQ1,subQ0]});Q24=makeQuery(id+"F6.imprint","IMPRINT",FACE,{"disambiguationData":[TD([[makeQuery(id+"F6.imprint","IMPRINT",EDGE,{"disambiguationData":[TD([[subQ2,-1.0]])],"derivedFrom":subQ1}),-1.0]])]});}
            var Q25;
            {var subQ0=sQuery(id+"F6.wireOp",EDGE,"E50");var subQ1=sQuery(id+"F6.wireOp",EDGE,"E44");var subQ2=makeQuery(id+"F6.imprint","INTERSECT",VERTEX,{"derivedFrom":[subQ1,subQ0]});Q25=makeQuery(id+"F6.imprint","IMPRINT",FACE,{"disambiguationData":[TD([[makeQuery(id+"F6.imprint","IMPRINT",EDGE,{"disambiguationData":[TD([[subQ2,-1.0]])],"derivedFrom":subQ1}),-1.0]])]});}
            var Q26;
            {var subQ0=sQuery(id+"F6.wireOp",EDGE,"E44");var subQ1=sQuery(id+"F6.wireOp",EDGE,"E29.right");var subQ2=makeQuery(id+"F6.imprint","INTERSECT",VERTEX,{"derivedFrom":[subQ1,subQ0]});Q26=makeQuery(id+"F6.imprint","IMPRINT",FACE,{"disambiguationData":[TD([[makeQuery(id+"F6.imprint","IMPRINT",EDGE,{"disambiguationData":[TD([[subQ2,-1.0]])],"derivedFrom":subQ1}),1.0]])]});}
            var Q27;
            {var subQ0=sQuery(id+"F6.wireOp",EDGE,"E45");var subQ1=sQuery(id+"F6.wireOp",EDGE,"E29.right");var subQ2=makeQuery(id+"F6.imprint","INTERSECT",VERTEX,{"derivedFrom":[subQ1,subQ0]});Q27=makeQuery(id+"F6.imprint","IMPRINT",FACE,{"disambiguationData":[TD([[makeQuery(id+"F6.imprint","IMPRINT",EDGE,{"disambiguationData":[TD([[subQ2,-1.0]])],"derivedFrom":subQ1}),1.0]])]});}
            var Q28;
            {var subQ0=sQuery(id+"F6.wireOp",EDGE,"E50");var subQ1=sQuery(id+"F6.wireOp",EDGE,"E45");var subQ2=makeQuery(id+"F6.imprint","INTERSECT",VERTEX,{"derivedFrom":[subQ1,subQ0]});Q28=makeQuery(id+"F6.imprint","IMPRINT",FACE,{"disambiguationData":[TD([[makeQuery(id+"F6.imprint","IMPRINT",EDGE,{"disambiguationData":[TD([[subQ2,-1.0]])],"derivedFrom":subQ1}),-1.0]])]});}
            var Q29;
            {var subQ0=sQuery(id+"F6.wireOp",EDGE,"E45");var subQ1=sQuery(id+"F6.wireOp",EDGE,"E29.left");var subQ2=makeQuery(id+"F6.imprint","INTERSECT",VERTEX,{"derivedFrom":[subQ1,subQ0]});Q29=makeQuery(id+"F6.imprint","IMPRINT",FACE,{"disambiguationData":[TD([[makeQuery(id+"F6.imprint","IMPRINT",EDGE,{"disambiguationData":[TD([[subQ2,-1.0]])],"derivedFrom":subQ1}),-1.0]])]});}
            var Q30;
            {var subQ0=sQuery(id+"F6.wireOp",EDGE,"E46");var subQ1=sQuery(id+"F6.wireOp",EDGE,"E29.left");var subQ2=makeQuery(id+"F6.imprint","INTERSECT",VERTEX,{"derivedFrom":[subQ1,subQ0]});Q30=makeQuery(id+"F6.imprint","IMPRINT",FACE,{"disambiguationData":[TD([[makeQuery(id+"F6.imprint","IMPRINT",EDGE,{"disambiguationData":[TD([[subQ2,-1.0]])],"derivedFrom":subQ1}),-1.0]])]});}
            var Q31;
            {var subQ0=sQuery(id+"F6.wireOp",EDGE,"E50");var subQ1=sQuery(id+"F6.wireOp",EDGE,"E46");var subQ2=makeQuery(id+"F6.imprint","INTERSECT",VERTEX,{"derivedFrom":[subQ1,subQ0]});Q31=makeQuery(id+"F6.imprint","IMPRINT",FACE,{"disambiguationData":[TD([[makeQuery(id+"F6.imprint","IMPRINT",EDGE,{"disambiguationData":[TD([[subQ2,-1.0]])],"derivedFrom":subQ1}),-1.0]])]});}
            var Q32;
            {var subQ0=sQuery(id+"F6.wireOp",EDGE,"E46");var subQ1=sQuery(id+"F6.wireOp",EDGE,"E29.right");var subQ2=makeQuery(id+"F6.imprint","INTERSECT",VERTEX,{"derivedFrom":[subQ1,subQ0]});Q32=makeQuery(id+"F6.imprint","IMPRINT",FACE,{"disambiguationData":[TD([[makeQuery(id+"F6.imprint","IMPRINT",EDGE,{"disambiguationData":[TD([[subQ2,-1.0]])],"derivedFrom":subQ1}),1.0]])]});}
            var Q33;
            {var subQ0=sQuery(id+"F6.wireOp",EDGE,"E47");var subQ1=sQuery(id+"F6.wireOp",EDGE,"E29.right");var subQ2=makeQuery(id+"F6.imprint","INTERSECT",VERTEX,{"derivedFrom":[subQ1,subQ0]});Q33=makeQuery(id+"F6.imprint","IMPRINT",FACE,{"disambiguationData":[TD([[makeQuery(id+"F6.imprint","IMPRINT",EDGE,{"disambiguationData":[TD([[subQ2,-1.0]])],"derivedFrom":subQ1}),1.0]])]});}
            var Q34;
            {var subQ0=sQuery(id+"F6.wireOp",EDGE,"E50");var subQ1=sQuery(id+"F6.wireOp",EDGE,"E47");var subQ2=makeQuery(id+"F6.imprint","INTERSECT",VERTEX,{"derivedFrom":[subQ1,subQ0]});Q34=makeQuery(id+"F6.imprint","IMPRINT",FACE,{"disambiguationData":[TD([[makeQuery(id+"F6.imprint","IMPRINT",EDGE,{"disambiguationData":[TD([[subQ2,-1.0]])],"derivedFrom":subQ1}),-1.0]])]});}
            var Q35;
            {var subQ0=sQuery(id+"F6.wireOp",EDGE,"E47");var subQ1=sQuery(id+"F6.wireOp",EDGE,"E29.left");var subQ2=makeQuery(id+"F6.imprint","INTERSECT",VERTEX,{"derivedFrom":[subQ1,subQ0]});Q35=makeQuery(id+"F6.imprint","IMPRINT",FACE,{"disambiguationData":[TD([[makeQuery(id+"F6.imprint","IMPRINT",EDGE,{"disambiguationData":[TD([[subQ2,-1.0]])],"derivedFrom":subQ1}),-1.0]])]});}
            var Q36;
            {var subQ0=sQuery(id+"F6.wireOp",EDGE,"E29.left");var subQ5=sQuery(id+"F6.wireOp",EDGE,"E48");var subQ6=makeQuery(id+"F6.imprint","INTERSECT",VERTEX,{"derivedFrom":[subQ0,subQ5]});Q36=makeQuery(id+"F6.imprint","IMPRINT",FACE,{"disambiguationData":[TD([[makeQuery(id+"F6.imprint","IMPRINT",EDGE,{"disambiguationData":[TD([[subQ6,1.0]])],"derivedFrom":subQ5}),-1.0]])]});}
            var Q37;
            {var subQ0=sQuery(id+"F6.wireOp",EDGE,"E50");var subQ1=sQuery(id+"F6.wireOp",EDGE,"E29.top");var subQ2=makeQuery(id+"F6.imprint","INTERSECT",VERTEX,{"derivedFrom":[subQ1,subQ0]});Q37=makeQuery(id+"F6.imprint","IMPRINT",FACE,{"disambiguationData":[TD([[makeQuery(id+"F6.imprint","IMPRINT",EDGE,{"disambiguationData":[TD([[subQ2,1.0]])],"derivedFrom":subQ1}),-1.0]])]});}
            var Q38;
            {var subQ0=sQuery(id+"F6.wireOp",EDGE,"E29.right");var subQ2=sQuery(id+"F6.wireOp",EDGE,"E29.top");var subQ3=makeQuery(id+"F6.imprint","INTERSECT",VERTEX,{"derivedFrom":[subQ2,subQ0]});Q38=makeQuery(id+"F6.imprint","IMPRINT",FACE,{"disambiguationData":[TD([[makeQuery(id+"F6.imprint","IMPRINT",EDGE,{"disambiguationData":[TD([[subQ3,1.0]])],"derivedFrom":subQ2}),-1.0]])]});}
            extrude(context, id + "F7", {"entities" : qUnion([Q0, Q1, Q2, Q3, Q4, Q5, Q6, Q7, Q8, Q9, Q10, Q11, Q12, Q13, Q14, Q15, Q16, Q17, Q18, Q19, Q20, Q21, Q22, Q23, Q24, Q25, Q26, Q27, Q28, Q29, Q30, Q31, Q32, Q33, Q34, Q35, Q36, Q37, Q38]), "depth" : 2.5 * mm, "offsetDistance" : 25.4 * mm});
        }
        {
            var Q0;
            Q0=makeQuery(id+"F7.opExtrude","CAP_FACE",FACE,{"disambiguationData":[OSD([sQuery(id+"F6.wireOp",EDGE,"E28.bottom"),sQuery(id+"F6.wireOp",EDGE,"E28.top"),sQuery(id+"F6.wireOp",EDGE,"E28.left"),sQuery(id+"F6.wireOp",EDGE,"E28.right")])],"isStart":false});
            var sketch = newSketch(context, id + "F8", { "sketchPlane" : qUnion([Q0])});
            skLineSegment(sketch, "E62.0", {"start": v(-23.53, 2.84) * mm, "end": v(-15.53, 2.84) * mm});
            skLineSegment(sketch, "E62.1", {"start": v(-23.53, 2.84) * mm, "end": v(-23.53, -11.66) * mm});
            skLineSegment(sketch, "E62.2", {"start": v(-23.53, -0.06) * mm, "end": v(-15.53, -0.06) * mm});
            skLineSegment(sketch, "E62.3", {"start": v(-23.53, -2.96) * mm, "end": v(-15.53, -2.96) * mm});
            skLineSegment(sketch, "E62.4", {"start": v(-18.22, -11.66) * mm, "end": v(-18.22, 2.84) * mm});
            skLineSegment(sketch, "E62.5", {"start": v(-20.91, 2.84) * mm, "end": v(-20.91, -11.66) * mm});
            skLineSegment(sketch, "E62.6", {"start": v(-15.53, 6.09) * mm, "end": v(-15.53, -17.16) * mm});
            skLineSegment(sketch, "E62.8", {"start": v(-23.53, -8.76) * mm, "end": v(-15.53, -8.76) * mm});
            skLineSegment(sketch, "E62.9", {"start": v(-23.53, -5.86) * mm, "end": v(-15.53, -5.86) * mm});
            skLineSegment(sketch, "E63.0", {"start": v(28.47, 5.09) * mm, "end": v(20.47, 5.09) * mm});
            skLineSegment(sketch, "E63.1", {"start": v(20.47, 2.15) * mm, "end": v(28.47, 2.15) * mm});
            skLineSegment(sketch, "E63.2", {"start": v(20.47, -0.79) * mm, "end": v(28.47, -0.79) * mm});
            skLineSegment(sketch, "E63.3", {"start": v(20.47, -3.73) * mm, "end": v(28.47, -3.73) * mm});
            skLineSegment(sketch, "E63.4", {"start": v(20.47, -6.66) * mm, "end": v(28.47, -6.66) * mm});
            skLineSegment(sketch, "E63.5", {"start": v(20.47, -9.6) * mm, "end": v(28.47, -9.6) * mm});
            skLineSegment(sketch, "E63.6", {"start": v(20.47, -12.54) * mm, "end": v(28.47, -12.54) * mm});
            skLineSegment(sketch, "E63.7", {"start": v(20.47, -15.48) * mm, "end": v(28.47, -15.48) * mm});
            skLineSegment(sketch, "E63.8", {"start": v(28.47, -18.41) * mm, "end": v(20.47, -18.41) * mm});
            skLineSegment(sketch, "E63.9", {"start": v(25.8, -18.41) * mm, "end": v(25.8, 5.09) * mm});
            skLineSegment(sketch, "E63.10", {"start": v(28.47, 5.09) * mm, "end": v(28.47, -18.41) * mm});
            skLineSegment(sketch, "E63.11", {"start": v(23.13, 5.09) * mm, "end": v(23.13, -18.41) * mm});
            skLineSegment(sketch, "E63.12", {"start": v(20.47, 5.09) * mm, "end": v(20.47, -18.41) * mm});
            skLineSegment(sketch, "E64.0", {"start": v(-23.53, -0.06) * mm, "end": v(-20.91, 2.84) * mm, "construction": true});
            skLineSegment(sketch, "E64.1", {"start": v(-23.53, -0.06) * mm, "end": v(-20.91, -2.96) * mm, "construction": true});
            skLineSegment(sketch, "E64.2", {"start": v(-20.91, -2.96) * mm, "end": v(-23.53, -5.86) * mm, "construction": true});
            skLineSegment(sketch, "E64.3", {"start": v(-20.91, -8.76) * mm, "end": v(-23.53, -5.86) * mm, "construction": true});
            skLineSegment(sketch, "E64.4", {"start": v(-20.91, -8.76) * mm, "end": v(-23.53, -11.66) * mm, "construction": true});
            skLineSegment(sketch, "E65.bottom", {"start": v(-21.72, 1.94) * mm, "end": v(-22.72, 1.94) * mm});
            skLineSegment(sketch, "E65.top", {"start": v(-21.72, 0.83) * mm, "end": v(-22.72, 0.83) * mm});
            skLineSegment(sketch, "E65.left", {"start": v(-21.72, 1.94) * mm, "end": v(-21.72, 0.83) * mm});
            skPoint(sketch, "E65.middle", {"position": v(-22.22, 1.39) * mm});
            skLineSegment(sketch, "E66.bottom", {"start": v(-21.72, -0.96) * mm, "end": v(-22.72, -0.96) * mm});
            skLineSegment(sketch, "E66.top", {"start": v(-21.72, -2.07) * mm, "end": v(-22.72, -2.07) * mm});
            skLineSegment(sketch, "E66.left", {"start": v(-21.72, -0.96) * mm, "end": v(-21.72, -2.07) * mm});
            skLineSegment(sketch, "E66.right", {"start": v(-22.72, -0.96) * mm, "end": v(-22.72, -2.07) * mm});
            skPoint(sketch, "E66.middle", {"position": v(-22.22, -1.51) * mm});
            skLineSegment(sketch, "E67.bottom", {"start": v(-21.72, -3.86) * mm, "end": v(-22.72, -3.86) * mm});
            skLineSegment(sketch, "E67.top", {"start": v(-21.72, -4.97) * mm, "end": v(-22.72, -4.97) * mm});
            skLineSegment(sketch, "E67.left", {"start": v(-21.72, -3.86) * mm, "end": v(-21.72, -4.97) * mm});
            skLineSegment(sketch, "E67.right", {"start": v(-22.72, -3.86) * mm, "end": v(-22.72, -4.97) * mm});
            skPoint(sketch, "E67.middle", {"position": v(-22.22, -4.41) * mm});
            skLineSegment(sketch, "E68.bottom", {"start": v(-21.72, -6.76) * mm, "end": v(-22.72, -6.76) * mm});
            skLineSegment(sketch, "E68.top", {"start": v(-21.72, -7.87) * mm, "end": v(-22.72, -7.87) * mm});
            skLineSegment(sketch, "E68.left", {"start": v(-21.72, -6.76) * mm, "end": v(-21.72, -7.87) * mm});
            skLineSegment(sketch, "E68.right", {"start": v(-22.72, -6.76) * mm, "end": v(-22.72, -7.87) * mm});
            skPoint(sketch, "E68.middle", {"position": v(-22.22, -7.31) * mm});
            skLineSegment(sketch, "E69.bottom", {"start": v(-21.72, -9.66) * mm, "end": v(-22.72, -9.66) * mm});
            skLineSegment(sketch, "E69.top", {"start": v(-21.72, -10.77) * mm, "end": v(-22.72, -10.77) * mm});
            skLineSegment(sketch, "E69.left", {"start": v(-21.72, -9.66) * mm, "end": v(-21.72, -10.77) * mm});
            skLineSegment(sketch, "E69.right", {"start": v(-22.72, -9.66) * mm, "end": v(-22.72, -10.77) * mm});
            skPoint(sketch, "E69.middle", {"position": v(-22.22, -10.21) * mm});
            skLineSegment(sketch, "E70", {"start": v(-22.72, 0.83) * mm, "end": v(-22.72, 1.94) * mm});
            skLineSegment(sketch, "E71.MirrorCS", {"start": v(-20.1, 0.83) * mm, "end": v(-19.1, 0.83) * mm});
            skLineSegment(sketch, "E72.MirrorCS", {"start": v(-20.1, 1.94) * mm, "end": v(-20.1, 0.83) * mm});
            skLineSegment(sketch, "E73.MirrorCS", {"start": v(-20.1, 1.94) * mm, "end": v(-19.1, 1.94) * mm});
            skLineSegment(sketch, "E74.MirrorCS", {"start": v(-19.1, 0.83) * mm, "end": v(-19.1, 1.94) * mm});
            skLineSegment(sketch, "E75.MirrorCS", {"start": v(-20.1, -0.96) * mm, "end": v(-19.1, -0.96) * mm});
            skLineSegment(sketch, "E76.MirrorCS", {"start": v(-20.1, -0.96) * mm, "end": v(-20.1, -2.07) * mm});
            skLineSegment(sketch, "E77.MirrorCS", {"start": v(-20.1, -2.07) * mm, "end": v(-19.1, -2.07) * mm});
            skLineSegment(sketch, "E78.MirrorCS", {"start": v(-19.1, -0.96) * mm, "end": v(-19.1, -2.07) * mm});
            skLineSegment(sketch, "E79.MirrorCS", {"start": v(-20.1, -3.86) * mm, "end": v(-19.1, -3.86) * mm});
            skLineSegment(sketch, "E80.MirrorCS", {"start": v(-19.1, -3.86) * mm, "end": v(-19.1, -4.97) * mm});
            skLineSegment(sketch, "E81.MirrorCS", {"start": v(-20.1, -4.97) * mm, "end": v(-19.1, -4.97) * mm});
            skLineSegment(sketch, "E82.MirrorCS", {"start": v(-20.1, -3.86) * mm, "end": v(-20.1, -4.97) * mm});
            skLineSegment(sketch, "E83.MirrorCS", {"start": v(-20.1, -6.76) * mm, "end": v(-19.1, -6.76) * mm});
            skLineSegment(sketch, "E84.MirrorCS", {"start": v(-20.1, -6.76) * mm, "end": v(-20.1, -7.87) * mm});
            skLineSegment(sketch, "E85.MirrorCS", {"start": v(-20.1, -7.87) * mm, "end": v(-19.1, -7.87) * mm});
            skLineSegment(sketch, "E86.MirrorCS", {"start": v(-19.1, -6.76) * mm, "end": v(-19.1, -7.87) * mm});
            skLineSegment(sketch, "E87.MirrorCS", {"start": v(-20.1, -9.66) * mm, "end": v(-19.1, -9.66) * mm});
            skLineSegment(sketch, "E88.MirrorCS", {"start": v(-19.1, -9.66) * mm, "end": v(-19.1, -10.77) * mm});
            skLineSegment(sketch, "E89.MirrorCS", {"start": v(-20.1, -10.77) * mm, "end": v(-19.1, -10.77) * mm});
            skLineSegment(sketch, "E90.MirrorCS", {"start": v(-20.1, -9.66) * mm, "end": v(-20.1, -10.77) * mm});
            skLineSegment(sketch, "E91.MirrorCS", {"start": v(-17.34, 0.83) * mm, "end": v(-17.34, 1.94) * mm});
            skLineSegment(sketch, "E92.MirrorCS", {"start": v(-16.34, 1.94) * mm, "end": v(-17.34, 1.94) * mm});
            skLineSegment(sketch, "E93.MirrorCS", {"start": v(-16.34, 1.94) * mm, "end": v(-16.34, 0.83) * mm});
            skLineSegment(sketch, "E94.MirrorCS", {"start": v(-16.34, 0.83) * mm, "end": v(-17.34, 0.83) * mm});
            skLineSegment(sketch, "E95.MirrorCS", {"start": v(-16.34, -2.07) * mm, "end": v(-17.34, -2.07) * mm});
            skLineSegment(sketch, "E96.MirrorCS", {"start": v(-17.34, -0.96) * mm, "end": v(-17.34, -2.07) * mm});
            skLineSegment(sketch, "E97.MirrorCS", {"start": v(-16.34, -0.96) * mm, "end": v(-17.34, -0.96) * mm});
            skLineSegment(sketch, "E98.MirrorCS", {"start": v(-16.34, -0.96) * mm, "end": v(-16.34, -2.07) * mm});
            skLineSegment(sketch, "E99.MirrorCS", {"start": v(-16.34, -3.86) * mm, "end": v(-17.34, -3.86) * mm});
            skLineSegment(sketch, "E100.MirrorCS", {"start": v(-16.34, -3.86) * mm, "end": v(-16.34, -4.97) * mm});
            skLineSegment(sketch, "E101.MirrorCS", {"start": v(-16.34, -4.97) * mm, "end": v(-17.34, -4.97) * mm});
            skLineSegment(sketch, "E102.MirrorCS", {"start": v(-17.34, -3.86) * mm, "end": v(-17.34, -4.97) * mm});
            skLineSegment(sketch, "E103.MirrorCS", {"start": v(-16.34, -6.76) * mm, "end": v(-17.34, -6.76) * mm});
            skLineSegment(sketch, "E104.MirrorCS", {"start": v(-17.34, -6.76) * mm, "end": v(-17.34, -7.87) * mm});
            skLineSegment(sketch, "E105.MirrorCS", {"start": v(-16.34, -7.87) * mm, "end": v(-17.34, -7.87) * mm});
            skLineSegment(sketch, "E106.MirrorCS", {"start": v(-16.34, -6.76) * mm, "end": v(-16.34, -7.87) * mm});
            skLineSegment(sketch, "E107.MirrorCS", {"start": v(-16.34, -9.66) * mm, "end": v(-17.34, -9.66) * mm});
            skLineSegment(sketch, "E108.MirrorCS", {"start": v(-16.34, -9.66) * mm, "end": v(-16.34, -10.77) * mm});
            skLineSegment(sketch, "E109.MirrorCS", {"start": v(-16.34, -10.77) * mm, "end": v(-17.34, -10.77) * mm});
            skLineSegment(sketch, "E110.MirrorCS", {"start": v(-17.34, -9.66) * mm, "end": v(-17.34, -10.77) * mm});
            skLineSegment(sketch, "E111.0", {"start": v(20.47, 5.09) * mm, "end": v(23.13, 2.15) * mm, "construction": true});
            skLineSegment(sketch, "E111.1", {"start": v(23.13, 2.15) * mm, "end": v(20.47, -0.79) * mm, "construction": true});
            skLineSegment(sketch, "E111.2", {"start": v(20.47, -0.79) * mm, "end": v(23.13, -3.73) * mm, "construction": true});
            skLineSegment(sketch, "E111.3", {"start": v(23.13, -3.73) * mm, "end": v(20.47, -6.66) * mm, "construction": true});
            skLineSegment(sketch, "E111.4", {"start": v(20.47, -6.66) * mm, "end": v(23.13, -9.6) * mm, "construction": true});
            skLineSegment(sketch, "E111.5", {"start": v(23.13, -9.6) * mm, "end": v(20.47, -12.54) * mm, "construction": true});
            skLineSegment(sketch, "E111.6", {"start": v(20.47, -12.54) * mm, "end": v(23.13, -15.48) * mm, "construction": true});
            skLineSegment(sketch, "E111.7", {"start": v(23.13, -15.48) * mm, "end": v(20.47, -18.41) * mm, "construction": true});
            skLineSegment(sketch, "E112.bottom", {"start": v(21.3, 4.17) * mm, "end": v(22.3, 4.17) * mm});
            skLineSegment(sketch, "E112.top", {"start": v(21.3, 3.07) * mm, "end": v(22.3, 3.07) * mm});
            skLineSegment(sketch, "E112.left", {"start": v(21.3, 4.17) * mm, "end": v(21.3, 3.07) * mm});
            skLineSegment(sketch, "E112.right", {"start": v(22.3, 4.17) * mm, "end": v(22.3, 3.07) * mm});
            skPoint(sketch, "E112.middle", {"position": v(21.8, 3.62) * mm});
            skLineSegment(sketch, "E113.bottom", {"start": v(22.3, 1.23) * mm, "end": v(21.3, 1.23) * mm});
            skLineSegment(sketch, "E113.top", {"start": v(22.3, 0.13) * mm, "end": v(21.3, 0.13) * mm});
            skLineSegment(sketch, "E113.left", {"start": v(22.3, 1.23) * mm, "end": v(22.3, 0.13) * mm});
            skLineSegment(sketch, "E113.right", {"start": v(21.3, 1.23) * mm, "end": v(21.3, 0.13) * mm});
            skPoint(sketch, "E113.middle", {"position": v(21.8, 0.68) * mm});
            skLineSegment(sketch, "E114.bottom", {"start": v(21.3, -1.7) * mm, "end": v(22.3, -1.7) * mm});
            skLineSegment(sketch, "E114.top", {"start": v(21.3, -2.8) * mm, "end": v(22.3, -2.8) * mm});
            skLineSegment(sketch, "E114.left", {"start": v(21.3, -1.7) * mm, "end": v(21.3, -2.8) * mm});
            skLineSegment(sketch, "E114.right", {"start": v(22.3, -1.7) * mm, "end": v(22.3, -2.8) * mm});
            skPoint(sketch, "E114.middle", {"position": v(21.8, -2.26) * mm});
            skLineSegment(sketch, "E115.bottom", {"start": v(22.3, -4.65) * mm, "end": v(21.3, -4.65) * mm});
            skLineSegment(sketch, "E115.top", {"start": v(22.3, -5.75) * mm, "end": v(21.3, -5.75) * mm});
            skLineSegment(sketch, "E115.left", {"start": v(22.3, -4.65) * mm, "end": v(22.3, -5.75) * mm});
            skLineSegment(sketch, "E115.right", {"start": v(21.3, -4.65) * mm, "end": v(21.3, -5.75) * mm});
            skPoint(sketch, "E115.middle", {"position": v(21.8, -5.2) * mm});
            skLineSegment(sketch, "E116.bottom", {"start": v(21.3, -7.58) * mm, "end": v(22.3, -7.58) * mm});
            skLineSegment(sketch, "E116.top", {"start": v(21.3, -8.68) * mm, "end": v(22.3, -8.68) * mm});
            skLineSegment(sketch, "E116.left", {"start": v(21.3, -7.58) * mm, "end": v(21.3, -8.68) * mm});
            skLineSegment(sketch, "E116.right", {"start": v(22.3, -7.58) * mm, "end": v(22.3, -8.68) * mm});
            skPoint(sketch, "E116.middle", {"position": v(21.8, -8.13) * mm});
            skLineSegment(sketch, "E117.bottom", {"start": v(22.3, -10.52) * mm, "end": v(21.3, -10.52) * mm});
            skLineSegment(sketch, "E117.top", {"start": v(22.3, -11.62) * mm, "end": v(21.3, -11.62) * mm});
            skLineSegment(sketch, "E117.left", {"start": v(22.3, -10.52) * mm, "end": v(22.3, -11.62) * mm});
            skLineSegment(sketch, "E117.right", {"start": v(21.3, -10.52) * mm, "end": v(21.3, -11.62) * mm});
            skPoint(sketch, "E117.middle", {"position": v(21.8, -11.07) * mm});
            skLineSegment(sketch, "E118.bottom", {"start": v(21.3, -13.46) * mm, "end": v(22.3, -13.46) * mm});
            skLineSegment(sketch, "E118.top", {"start": v(21.3, -14.56) * mm, "end": v(22.3, -14.56) * mm});
            skLineSegment(sketch, "E118.left", {"start": v(21.3, -13.46) * mm, "end": v(21.3, -14.56) * mm});
            skLineSegment(sketch, "E118.right", {"start": v(22.3, -13.46) * mm, "end": v(22.3, -14.56) * mm});
            skPoint(sketch, "E118.middle", {"position": v(21.8, -14) * mm});
            skLineSegment(sketch, "E119.bottom", {"start": v(22.3, -16.4) * mm, "end": v(21.3, -16.4) * mm});
            skLineSegment(sketch, "E119.top", {"start": v(22.3, -17.5) * mm, "end": v(21.3, -17.5) * mm});
            skLineSegment(sketch, "E119.left", {"start": v(22.3, -16.4) * mm, "end": v(22.3, -17.5) * mm});
            skLineSegment(sketch, "E119.right", {"start": v(21.3, -16.4) * mm, "end": v(21.3, -17.5) * mm});
            skPoint(sketch, "E119.middle", {"position": v(21.8, -16.95) * mm});
            skLineSegment(sketch, "E120.MirrorCS", {"start": v(24.97, 4.17) * mm, "end": v(23.97, 4.17) * mm});
            skLineSegment(sketch, "E121.MirrorCS", {"start": v(24.97, 4.17) * mm, "end": v(24.97, 3.07) * mm});
            skLineSegment(sketch, "E122.MirrorCS", {"start": v(24.97, 3.07) * mm, "end": v(23.97, 3.07) * mm});
            skLineSegment(sketch, "E123.MirrorCS", {"start": v(23.97, 4.17) * mm, "end": v(23.97, 3.07) * mm});
            skLineSegment(sketch, "E124.MirrorCS", {"start": v(23.97, 1.23) * mm, "end": v(24.97, 1.23) * mm});
            skLineSegment(sketch, "E125.MirrorCS", {"start": v(24.97, 1.23) * mm, "end": v(24.97, 0.13) * mm});
            skLineSegment(sketch, "E126.MirrorCS", {"start": v(23.97, 0.13) * mm, "end": v(24.97, 0.13) * mm});
            skLineSegment(sketch, "E127.MirrorCS", {"start": v(23.97, 1.23) * mm, "end": v(23.97, 0.13) * mm});
            skLineSegment(sketch, "E128.MirrorCS", {"start": v(24.97, -1.7) * mm, "end": v(23.97, -1.7) * mm});
            skLineSegment(sketch, "E129.MirrorCS", {"start": v(24.97, -1.7) * mm, "end": v(24.97, -2.8) * mm});
            skLineSegment(sketch, "E130.MirrorCS", {"start": v(24.97, -2.8) * mm, "end": v(23.97, -2.8) * mm});
            skLineSegment(sketch, "E131.MirrorCS", {"start": v(23.97, -1.7) * mm, "end": v(23.97, -2.8) * mm});
            skLineSegment(sketch, "E132.MirrorCS", {"start": v(23.97, -4.65) * mm, "end": v(24.97, -4.65) * mm});
            skLineSegment(sketch, "E133.MirrorCS", {"start": v(24.97, -4.65) * mm, "end": v(24.97, -5.75) * mm});
            skLineSegment(sketch, "E134.MirrorCS", {"start": v(23.97, -5.75) * mm, "end": v(24.97, -5.75) * mm});
            skLineSegment(sketch, "E135.MirrorCS", {"start": v(23.97, -4.65) * mm, "end": v(23.97, -5.75) * mm});
            skLineSegment(sketch, "E136.MirrorCS", {"start": v(24.97, -7.58) * mm, "end": v(23.97, -7.58) * mm});
            skLineSegment(sketch, "E137.MirrorCS", {"start": v(24.97, -7.58) * mm, "end": v(24.97, -8.68) * mm});
            skLineSegment(sketch, "E138.MirrorCS", {"start": v(24.97, -8.68) * mm, "end": v(23.97, -8.68) * mm});
            skLineSegment(sketch, "E139.MirrorCS", {"start": v(23.97, -7.58) * mm, "end": v(23.97, -8.68) * mm});
            skLineSegment(sketch, "E140.MirrorCS", {"start": v(23.97, -10.52) * mm, "end": v(24.97, -10.52) * mm});
            skLineSegment(sketch, "E141.MirrorCS", {"start": v(24.97, -10.52) * mm, "end": v(24.97, -11.62) * mm});
            skLineSegment(sketch, "E142.MirrorCS", {"start": v(23.97, -11.62) * mm, "end": v(24.97, -11.62) * mm});
            skLineSegment(sketch, "E143.MirrorCS", {"start": v(23.97, -10.52) * mm, "end": v(23.97, -11.62) * mm});
            skLineSegment(sketch, "E144.MirrorCS", {"start": v(24.97, -13.46) * mm, "end": v(23.97, -13.46) * mm});
            skLineSegment(sketch, "E145.MirrorCS", {"start": v(24.97, -13.46) * mm, "end": v(24.97, -14.56) * mm});
            skLineSegment(sketch, "E146.MirrorCS", {"start": v(24.97, -14.56) * mm, "end": v(23.97, -14.56) * mm});
            skLineSegment(sketch, "E147.MirrorCS", {"start": v(23.97, -13.46) * mm, "end": v(23.97, -14.56) * mm});
            skLineSegment(sketch, "E148.MirrorCS", {"start": v(23.97, -16.4) * mm, "end": v(24.97, -16.4) * mm});
            skLineSegment(sketch, "E149.MirrorCS", {"start": v(24.97, -16.4) * mm, "end": v(24.97, -17.5) * mm});
            skLineSegment(sketch, "E150.MirrorCS", {"start": v(23.97, -17.5) * mm, "end": v(24.97, -17.5) * mm});
            skLineSegment(sketch, "E151.MirrorCS", {"start": v(23.97, -16.4) * mm, "end": v(23.97, -17.5) * mm});
            skLineSegment(sketch, "E152.MirrorCS", {"start": v(26.63, 4.17) * mm, "end": v(27.63, 4.17) * mm});
            skLineSegment(sketch, "E153.MirrorCS", {"start": v(27.63, 4.17) * mm, "end": v(27.63, 3.07) * mm});
            skLineSegment(sketch, "E154.MirrorCS", {"start": v(26.63, 3.07) * mm, "end": v(27.63, 3.07) * mm});
            skLineSegment(sketch, "E155.MirrorCS", {"start": v(26.63, 4.17) * mm, "end": v(26.63, 3.07) * mm});
            skLineSegment(sketch, "E156.MirrorCS", {"start": v(27.63, 1.23) * mm, "end": v(26.63, 1.23) * mm});
            skLineSegment(sketch, "E157.MirrorCS", {"start": v(27.63, 1.23) * mm, "end": v(27.63, 0.13) * mm});
            skLineSegment(sketch, "E158.MirrorCS", {"start": v(27.63, 0.13) * mm, "end": v(26.63, 0.13) * mm});
            skLineSegment(sketch, "E159.MirrorCS", {"start": v(26.63, 1.23) * mm, "end": v(26.63, 0.13) * mm});
            skLineSegment(sketch, "E160.MirrorCS", {"start": v(26.63, -1.7) * mm, "end": v(27.63, -1.7) * mm});
            skLineSegment(sketch, "E161.MirrorCS", {"start": v(27.63, -1.7) * mm, "end": v(27.63, -2.8) * mm});
            skLineSegment(sketch, "E162.MirrorCS", {"start": v(26.63, -2.8) * mm, "end": v(27.63, -2.8) * mm});
            skLineSegment(sketch, "E163.MirrorCS", {"start": v(26.63, -1.7) * mm, "end": v(26.63, -2.8) * mm});
            skLineSegment(sketch, "E164.MirrorCS", {"start": v(27.63, -4.65) * mm, "end": v(26.63, -4.65) * mm});
            skLineSegment(sketch, "E165.MirrorCS", {"start": v(27.63, -4.65) * mm, "end": v(27.63, -5.75) * mm});
            skLineSegment(sketch, "E166.MirrorCS", {"start": v(27.63, -5.75) * mm, "end": v(26.63, -5.75) * mm});
            skLineSegment(sketch, "E167.MirrorCS", {"start": v(26.63, -4.65) * mm, "end": v(26.63, -5.75) * mm});
            skLineSegment(sketch, "E168.MirrorCS", {"start": v(26.63, -7.58) * mm, "end": v(27.63, -7.58) * mm});
            skLineSegment(sketch, "E169.MirrorCS", {"start": v(27.63, -7.58) * mm, "end": v(27.63, -8.68) * mm});
            skLineSegment(sketch, "E170.MirrorCS", {"start": v(26.63, -8.68) * mm, "end": v(27.63, -8.68) * mm});
            skLineSegment(sketch, "E171.MirrorCS", {"start": v(26.63, -7.58) * mm, "end": v(26.63, -8.68) * mm});
            skLineSegment(sketch, "E172.MirrorCS", {"start": v(26.63, -10.52) * mm, "end": v(26.63, -11.62) * mm});
            skLineSegment(sketch, "E173.MirrorCS", {"start": v(27.63, -10.52) * mm, "end": v(26.63, -10.52) * mm});
            skLineSegment(sketch, "E174.MirrorCS", {"start": v(27.63, -10.52) * mm, "end": v(27.63, -11.62) * mm});
            skLineSegment(sketch, "E175.MirrorCS", {"start": v(26.63, -13.46) * mm, "end": v(27.63, -13.46) * mm});
            skLineSegment(sketch, "E176.MirrorCS", {"start": v(27.63, -13.46) * mm, "end": v(27.63, -14.56) * mm});
            skLineSegment(sketch, "E177.MirrorCS", {"start": v(26.63, -14.56) * mm, "end": v(27.63, -14.56) * mm});
            skLineSegment(sketch, "E178.MirrorCS", {"start": v(26.63, -13.46) * mm, "end": v(26.63, -14.56) * mm});
            skLineSegment(sketch, "E179.MirrorCS", {"start": v(27.63, -16.4) * mm, "end": v(26.63, -16.4) * mm});
            skLineSegment(sketch, "E180.MirrorCS", {"start": v(27.63, -16.4) * mm, "end": v(27.63, -17.5) * mm});
            skLineSegment(sketch, "E181.MirrorCS", {"start": v(27.63, -17.5) * mm, "end": v(26.63, -17.5) * mm});
            skLineSegment(sketch, "E182.MirrorCS", {"start": v(26.63, -16.4) * mm, "end": v(26.63, -17.5) * mm});
            skLineSegment(sketch, "E183", {"start": v(26.63, -11.62) * mm, "end": v(27.63, -11.62) * mm});
            skSolve(sketch);
        }
        {
            var Q0;
            Q0=makeQuery(id+"F8.imprint","IMPRINT",FACE,{"disambiguationData":[TD([[makeQuery(id+"F8.imprint","IMPRINT",EDGE,{"derivedFrom":sQuery(id+"F8.wireOp",EDGE,"E65.bottom")}),1.0]])]});
            var Q1;
            Q1=makeQuery(id+"F8.imprint","IMPRINT",FACE,{"disambiguationData":[TD([[makeQuery(id+"F8.imprint","IMPRINT",EDGE,{"derivedFrom":sQuery(id+"F8.wireOp",EDGE,"E71.MirrorCS")}),1.0]])]});
            var Q2;
            Q2=makeQuery(id+"F8.imprint","IMPRINT",FACE,{"disambiguationData":[TD([[makeQuery(id+"F8.imprint","IMPRINT",EDGE,{"derivedFrom":sQuery(id+"F8.wireOp",EDGE,"E91.MirrorCS")}),-1.0]])]});
            var Q3;
            Q3=makeQuery(id+"F8.imprint","IMPRINT",FACE,{"disambiguationData":[TD([[makeQuery(id+"F8.imprint","IMPRINT",EDGE,{"derivedFrom":sQuery(id+"F8.wireOp",EDGE,"E95.MirrorCS")}),-1.0]])]});
            var Q4;
            Q4=makeQuery(id+"F8.imprint","IMPRINT",FACE,{"disambiguationData":[TD([[makeQuery(id+"F8.imprint","IMPRINT",EDGE,{"derivedFrom":sQuery(id+"F8.wireOp",EDGE,"E76.MirrorCS")}),1.0]])]});
            var Q5;
            Q5=makeQuery(id+"F8.imprint","IMPRINT",FACE,{"disambiguationData":[TD([[makeQuery(id+"F8.imprint","IMPRINT",EDGE,{"derivedFrom":sQuery(id+"F8.wireOp",EDGE,"E66.bottom")}),1.0]])]});
            var Q6;
            Q6=makeQuery(id+"F8.imprint","IMPRINT",FACE,{"disambiguationData":[TD([[makeQuery(id+"F8.imprint","IMPRINT",EDGE,{"derivedFrom":sQuery(id+"F8.wireOp",EDGE,"E67.bottom")}),1.0]])]});
            var Q7;
            Q7=makeQuery(id+"F8.imprint","IMPRINT",FACE,{"disambiguationData":[TD([[makeQuery(id+"F8.imprint","IMPRINT",EDGE,{"derivedFrom":sQuery(id+"F8.wireOp",EDGE,"E79.MirrorCS")}),-1.0]])]});
            var Q8;
            Q8=makeQuery(id+"F8.imprint","IMPRINT",FACE,{"disambiguationData":[TD([[makeQuery(id+"F8.imprint","IMPRINT",EDGE,{"derivedFrom":sQuery(id+"F8.wireOp",EDGE,"E99.MirrorCS")}),1.0]])]});
            var Q9;
            Q9=makeQuery(id+"F8.imprint","IMPRINT",FACE,{"disambiguationData":[TD([[makeQuery(id+"F8.imprint","IMPRINT",EDGE,{"derivedFrom":sQuery(id+"F8.wireOp",EDGE,"E103.MirrorCS")}),1.0]])]});
            var Q10;
            Q10=makeQuery(id+"F8.imprint","IMPRINT",FACE,{"disambiguationData":[TD([[makeQuery(id+"F8.imprint","IMPRINT",EDGE,{"derivedFrom":sQuery(id+"F8.wireOp",EDGE,"E83.MirrorCS")}),-1.0]])]});
            var Q11;
            Q11=makeQuery(id+"F8.imprint","IMPRINT",FACE,{"disambiguationData":[TD([[makeQuery(id+"F8.imprint","IMPRINT",EDGE,{"derivedFrom":sQuery(id+"F8.wireOp",EDGE,"E69.bottom")}),1.0]])]});
            var Q12;
            Q12=makeQuery(id+"F8.imprint","IMPRINT",FACE,{"disambiguationData":[TD([[makeQuery(id+"F8.imprint","IMPRINT",EDGE,{"derivedFrom":sQuery(id+"F8.wireOp",EDGE,"E87.MirrorCS")}),-1.0]])]});
            var Q13;
            Q13=makeQuery(id+"F8.imprint","IMPRINT",FACE,{"disambiguationData":[TD([[makeQuery(id+"F8.imprint","IMPRINT",EDGE,{"derivedFrom":sQuery(id+"F8.wireOp",EDGE,"E107.MirrorCS")}),1.0]])]});
            var Q14;
            Q14=makeQuery(id+"F8.imprint","IMPRINT",FACE,{"disambiguationData":[TD([[makeQuery(id+"F8.imprint","IMPRINT",EDGE,{"derivedFrom":sQuery(id+"F8.wireOp",EDGE,"E68.bottom")}),1.0]])]});
            var Q15;
            Q15=makeQuery(id+"F8.imprint","IMPRINT",FACE,{"disambiguationData":[TD([[makeQuery(id+"F8.imprint","IMPRINT",EDGE,{"derivedFrom":sQuery(id+"F8.wireOp",EDGE,"E112.bottom")}),-1.0]])]});
            var Q16;
            Q16=makeQuery(id+"F8.imprint","IMPRINT",FACE,{"disambiguationData":[TD([[makeQuery(id+"F8.imprint","IMPRINT",EDGE,{"derivedFrom":sQuery(id+"F8.wireOp",EDGE,"E120.MirrorCS")}),1.0]])]});
            var Q17;
            Q17=makeQuery(id+"F8.imprint","IMPRINT",FACE,{"disambiguationData":[TD([[makeQuery(id+"F8.imprint","IMPRINT",EDGE,{"derivedFrom":sQuery(id+"F8.wireOp",EDGE,"E152.MirrorCS")}),-1.0]])]});
            var Q18;
            Q18=makeQuery(id+"F8.imprint","IMPRINT",FACE,{"disambiguationData":[TD([[makeQuery(id+"F8.imprint","IMPRINT",EDGE,{"derivedFrom":sQuery(id+"F8.wireOp",EDGE,"E156.MirrorCS")}),1.0]])]});
            var Q19;
            Q19=makeQuery(id+"F8.imprint","IMPRINT",FACE,{"disambiguationData":[TD([[makeQuery(id+"F8.imprint","IMPRINT",EDGE,{"derivedFrom":sQuery(id+"F8.wireOp",EDGE,"E124.MirrorCS")}),-1.0]])]});
            var Q20;
            Q20=makeQuery(id+"F8.imprint","IMPRINT",FACE,{"disambiguationData":[TD([[makeQuery(id+"F8.imprint","IMPRINT",EDGE,{"derivedFrom":sQuery(id+"F8.wireOp",EDGE,"E113.bottom")}),1.0]])]});
            var Q21;
            Q21=makeQuery(id+"F8.imprint","IMPRINT",FACE,{"disambiguationData":[TD([[makeQuery(id+"F8.imprint","IMPRINT",EDGE,{"derivedFrom":sQuery(id+"F8.wireOp",EDGE,"E114.bottom")}),-1.0]])]});
            var Q22;
            Q22=makeQuery(id+"F8.imprint","IMPRINT",FACE,{"disambiguationData":[TD([[makeQuery(id+"F8.imprint","IMPRINT",EDGE,{"derivedFrom":sQuery(id+"F8.wireOp",EDGE,"E128.MirrorCS")}),1.0]])]});
            var Q23;
            Q23=makeQuery(id+"F8.imprint","IMPRINT",FACE,{"disambiguationData":[TD([[makeQuery(id+"F8.imprint","IMPRINT",EDGE,{"derivedFrom":sQuery(id+"F8.wireOp",EDGE,"E160.MirrorCS")}),-1.0]])]});
            var Q24;
            Q24=makeQuery(id+"F8.imprint","IMPRINT",FACE,{"disambiguationData":[TD([[makeQuery(id+"F8.imprint","IMPRINT",EDGE,{"derivedFrom":sQuery(id+"F8.wireOp",EDGE,"E164.MirrorCS")}),1.0]])]});
            var Q25;
            Q25=makeQuery(id+"F8.imprint","IMPRINT",FACE,{"disambiguationData":[TD([[makeQuery(id+"F8.imprint","IMPRINT",EDGE,{"derivedFrom":sQuery(id+"F8.wireOp",EDGE,"E132.MirrorCS")}),-1.0]])]});
            var Q26;
            Q26=makeQuery(id+"F8.imprint","IMPRINT",FACE,{"disambiguationData":[TD([[makeQuery(id+"F8.imprint","IMPRINT",EDGE,{"derivedFrom":sQuery(id+"F8.wireOp",EDGE,"E115.bottom")}),1.0]])]});
            var Q27;
            Q27=makeQuery(id+"F8.imprint","IMPRINT",FACE,{"disambiguationData":[TD([[makeQuery(id+"F8.imprint","IMPRINT",EDGE,{"derivedFrom":sQuery(id+"F8.wireOp",EDGE,"E116.bottom")}),-1.0]])]});
            var Q28;
            Q28=makeQuery(id+"F8.imprint","IMPRINT",FACE,{"disambiguationData":[TD([[makeQuery(id+"F8.imprint","IMPRINT",EDGE,{"derivedFrom":sQuery(id+"F8.wireOp",EDGE,"E136.MirrorCS")}),1.0]])]});
            var Q29;
            Q29=makeQuery(id+"F8.imprint","IMPRINT",FACE,{"disambiguationData":[TD([[makeQuery(id+"F8.imprint","IMPRINT",EDGE,{"derivedFrom":sQuery(id+"F8.wireOp",EDGE,"E168.MirrorCS")}),-1.0]])]});
            var Q30;
            Q30=makeQuery(id+"F8.imprint","IMPRINT",FACE,{"disambiguationData":[TD([[makeQuery(id+"F8.imprint","IMPRINT",EDGE,{"derivedFrom":sQuery(id+"F8.wireOp",EDGE,"E172.MirrorCS")}),1.0]])]});
            var Q31;
            Q31=makeQuery(id+"F8.imprint","IMPRINT",FACE,{"disambiguationData":[TD([[makeQuery(id+"F8.imprint","IMPRINT",EDGE,{"derivedFrom":sQuery(id+"F8.wireOp",EDGE,"E140.MirrorCS")}),-1.0]])]});
            var Q32;
            Q32=makeQuery(id+"F8.imprint","IMPRINT",FACE,{"disambiguationData":[TD([[makeQuery(id+"F8.imprint","IMPRINT",EDGE,{"derivedFrom":sQuery(id+"F8.wireOp",EDGE,"E117.bottom")}),1.0]])]});
            var Q33;
            Q33=makeQuery(id+"F8.imprint","IMPRINT",FACE,{"disambiguationData":[TD([[makeQuery(id+"F8.imprint","IMPRINT",EDGE,{"derivedFrom":sQuery(id+"F8.wireOp",EDGE,"E118.bottom")}),-1.0]])]});
            var Q34;
            Q34=makeQuery(id+"F8.imprint","IMPRINT",FACE,{"disambiguationData":[TD([[makeQuery(id+"F8.imprint","IMPRINT",EDGE,{"derivedFrom":sQuery(id+"F8.wireOp",EDGE,"E144.MirrorCS")}),1.0]])]});
            var Q35;
            Q35=makeQuery(id+"F8.imprint","IMPRINT",FACE,{"disambiguationData":[TD([[makeQuery(id+"F8.imprint","IMPRINT",EDGE,{"derivedFrom":sQuery(id+"F8.wireOp",EDGE,"E175.MirrorCS")}),-1.0]])]});
            var Q36;
            Q36=makeQuery(id+"F8.imprint","IMPRINT",FACE,{"disambiguationData":[TD([[makeQuery(id+"F8.imprint","IMPRINT",EDGE,{"derivedFrom":sQuery(id+"F8.wireOp",EDGE,"E179.MirrorCS")}),1.0]])]});
            var Q37;
            Q37=makeQuery(id+"F8.imprint","IMPRINT",FACE,{"disambiguationData":[TD([[makeQuery(id+"F8.imprint","IMPRINT",EDGE,{"derivedFrom":sQuery(id+"F8.wireOp",EDGE,"E148.MirrorCS")}),-1.0]])]});
            var Q38;
            Q38=makeQuery(id+"F8.imprint","IMPRINT",FACE,{"disambiguationData":[TD([[makeQuery(id+"F8.imprint","IMPRINT",EDGE,{"derivedFrom":sQuery(id+"F8.wireOp",EDGE,"E119.bottom")}),1.0]])]});
            extrude(context, id + "F9", {"entities" : qUnion([Q0, Q1, Q2, Q3, Q4, Q5, Q6, Q7, Q8, Q9, Q10, Q11, Q12, Q13, Q14, Q15, Q16, Q17, Q18, Q19, Q20, Q21, Q22, Q23, Q24, Q25, Q26, Q27, Q28, Q29, Q30, Q31, Q32, Q33, Q34, Q35, Q36, Q37, Q38]), "depth" : 6 * mm, "offsetDistance" : 25.4 * mm});
        }
        {
            var Q0;
            Q0=makeQuery(id+"F1.opExtrude","CAP_FACE",FACE,{"disambiguationData":[OSD([sQuery(id+"F0.wireOp",EDGE,"E0.bottom"),sQuery(id+"F0.wireOp",EDGE,"E0.top"),sQuery(id+"F0.wireOp",EDGE,"E0.left"),sQuery(id+"F0.wireOp",EDGE,"E0.right"),sQuery(id+"F0.wireOp",EDGE,"E14"),sQuery(id+"F0.wireOp",EDGE,"E15"),sQuery(id+"F0.wireOp",EDGE,"E16"),sQuery(id+"F0.wireOp",EDGE,"E17")])],"isStart":false});
            var sketch = newSketch(context, id + "F10", { "sketchPlane" : qUnion([Q0])});
            skLineSegment(sketch, "E184.0", {"start": v(-15.53, -17.16) * mm, "end": v(20.47, -17.16) * mm});
            skLineSegment(sketch, "E185", {"start": v(-15.53, -17.16) * mm, "end": v(-23.53, -17.16) * mm});
            skLineSegment(sketch, "E186.bottom", {"start": v(-9.03, -19.91) * mm, "end": v(-15.53, -19.91) * mm});
            skLineSegment(sketch, "E186.top", {"start": v(-9.03, -26.41) * mm, "end": v(-15.53, -26.41) * mm});
            skLineSegment(sketch, "E186.left", {"start": v(-9.03, -19.91) * mm, "end": v(-9.03, -26.41) * mm});
            skLineSegment(sketch, "E186.right", {"start": v(-15.53, -19.91) * mm, "end": v(-15.53, -26.41) * mm});
            skPoint(sketch, "E186.middle", {"position": v(-12.28, -23.16) * mm});
            skLineSegment(sketch, "E187.bottom", {"start": v(0.8, -19.91) * mm, "end": v(-5.7, -19.91) * mm});
            skLineSegment(sketch, "E187.top", {"start": v(0.8, -26.41) * mm, "end": v(-5.7, -26.41) * mm});
            skLineSegment(sketch, "E187.left", {"start": v(0.8, -19.91) * mm, "end": v(0.8, -26.41) * mm});
            skLineSegment(sketch, "E187.right", {"start": v(-5.7, -19.91) * mm, "end": v(-5.7, -26.41) * mm});
            skPoint(sketch, "E187.middle", {"position": v(-2.45, -23.16) * mm});
            skLineSegment(sketch, "E188.bottom", {"start": v(10.63, -19.91) * mm, "end": v(4.13, -19.91) * mm});
            skLineSegment(sketch, "E188.top", {"start": v(10.63, -26.41) * mm, "end": v(4.13, -26.41) * mm});
            skLineSegment(sketch, "E188.left", {"start": v(10.63, -19.91) * mm, "end": v(10.63, -26.41) * mm});
            skLineSegment(sketch, "E188.right", {"start": v(4.13, -19.91) * mm, "end": v(4.13, -26.41) * mm});
            skPoint(sketch, "E188.middle", {"position": v(7.38, -23.16) * mm});
            skLineSegment(sketch, "E189.bottom", {"start": v(20.47, -19.91) * mm, "end": v(13.97, -19.91) * mm});
            skLineSegment(sketch, "E189.top", {"start": v(20.47, -26.41) * mm, "end": v(13.97, -26.41) * mm});
            skLineSegment(sketch, "E189.left", {"start": v(20.47, -19.91) * mm, "end": v(20.47, -26.41) * mm});
            skLineSegment(sketch, "E189.right", {"start": v(13.97, -19.91) * mm, "end": v(13.97, -26.41) * mm});
            skPoint(sketch, "E189.middle", {"position": v(17.22, -23.16) * mm});
            skLineSegment(sketch, "E190", {"start": v(-23.53, -23.16) * mm, "end": v(28.47, -23.16) * mm});
            skLineSegment(sketch, "E191", {"start": v(-9.03, -18.89) * mm, "end": v(-5.7, -18.89) * mm});
            skLineSegment(sketch, "E192", {"start": v(0.8, -19.08) * mm, "end": v(4.13, -19.08) * mm});
            skLineSegment(sketch, "E193", {"start": v(10.63, -19.28) * mm, "end": v(13.97, -19.28) * mm});
            skSolve(sketch);
        }
        {
            var Q0;
            {var subQ0=sQuery(id+"F10.wireOp",EDGE,"E186.bottom");Q0=makeQuery(id+"F10.imprint","IMPRINT",FACE,{"disambiguationData":[TD([[makeQuery(id+"F10.imprint","IMPRINT",EDGE,{"derivedFrom":subQ0}),1.0]])]});}
            var Q1;
            {var subQ0=sQuery(id+"F10.wireOp",EDGE,"E186.top");Q1=makeQuery(id+"F10.imprint","IMPRINT",FACE,{"disambiguationData":[TD([[makeQuery(id+"F10.imprint","IMPRINT",EDGE,{"derivedFrom":subQ0}),-1.0]])]});}
            var Q2;
            {var subQ0=sQuery(id+"F10.wireOp",EDGE,"E187.bottom");Q2=makeQuery(id+"F10.imprint","IMPRINT",FACE,{"disambiguationData":[TD([[makeQuery(id+"F10.imprint","IMPRINT",EDGE,{"derivedFrom":subQ0}),1.0]])]});}
            var Q3;
            {var subQ0=sQuery(id+"F10.wireOp",EDGE,"E187.top");Q3=makeQuery(id+"F10.imprint","IMPRINT",FACE,{"disambiguationData":[TD([[makeQuery(id+"F10.imprint","IMPRINT",EDGE,{"derivedFrom":subQ0}),-1.0]])]});}
            var Q4;
            {var subQ0=sQuery(id+"F10.wireOp",EDGE,"E188.bottom");Q4=makeQuery(id+"F10.imprint","IMPRINT",FACE,{"disambiguationData":[TD([[makeQuery(id+"F10.imprint","IMPRINT",EDGE,{"derivedFrom":subQ0}),1.0]])]});}
            var Q5;
            {var subQ0=sQuery(id+"F10.wireOp",EDGE,"E188.top");Q5=makeQuery(id+"F10.imprint","IMPRINT",FACE,{"disambiguationData":[TD([[makeQuery(id+"F10.imprint","IMPRINT",EDGE,{"derivedFrom":subQ0}),-1.0]])]});}
            var Q6;
            {var subQ0=sQuery(id+"F10.wireOp",EDGE,"E189.bottom");Q6=makeQuery(id+"F10.imprint","IMPRINT",FACE,{"disambiguationData":[TD([[makeQuery(id+"F10.imprint","IMPRINT",EDGE,{"derivedFrom":subQ0}),1.0]])]});}
            var Q7;
            {var subQ0=sQuery(id+"F10.wireOp",EDGE,"E189.top");Q7=makeQuery(id+"F10.imprint","IMPRINT",FACE,{"disambiguationData":[TD([[makeQuery(id+"F10.imprint","IMPRINT",EDGE,{"derivedFrom":subQ0}),-1.0]])]});}
            extrude(context, id + "F11", {"entities" : qUnion([Q0, Q1, Q2, Q3, Q4, Q5, Q6, Q7]), "depth" : 2.5 * mm, "offsetDistance" : 25.4 * mm});
        }
        {
            var Q0;
            Q0=makeQuery(id+"F11.opExtrude","CAP_FACE",FACE,{"disambiguationData":[OSD([sQuery(id+"F10.wireOp",EDGE,"E186.bottom"),sQuery(id+"F10.wireOp",EDGE,"E186.top"),sQuery(id+"F10.wireOp",EDGE,"E186.left"),sQuery(id+"F10.wireOp",EDGE,"E186.right")])],"isStart":false});
            var sketch = newSketch(context, id + "F12", { "sketchPlane" : qUnion([Q0])});
            skLineSegment(sketch, "E194.1.0", {"start": v(-5.7, -19.91) * mm, "end": v(-5.7, -26.41) * mm});
            skLineSegment(sketch, "E194.1.1", {"start": v(-5.7, -26.41) * mm, "end": v(0.8, -26.41) * mm});
            skLineSegment(sketch, "E194.1.2", {"start": v(0.8, -26.41) * mm, "end": v(0.8, -19.91) * mm});
            skLineSegment(sketch, "E194.1.3", {"start": v(0.8, -19.91) * mm, "end": v(-5.7, -19.91) * mm});
            skLineSegment(sketch, "E194.2.0", {"start": v(4.13, -19.91) * mm, "end": v(4.13, -26.41) * mm});
            skLineSegment(sketch, "E194.2.1", {"start": v(4.13, -26.41) * mm, "end": v(10.63, -26.41) * mm});
            skLineSegment(sketch, "E194.2.2", {"start": v(10.63, -26.41) * mm, "end": v(10.63, -19.91) * mm});
            skLineSegment(sketch, "E194.2.3", {"start": v(10.63, -19.91) * mm, "end": v(4.13, -19.91) * mm});
            skLineSegment(sketch, "E194.3.0", {"start": v(13.97, -19.91) * mm, "end": v(13.97, -26.41) * mm});
            skLineSegment(sketch, "E194.3.1", {"start": v(13.97, -26.41) * mm, "end": v(20.47, -26.41) * mm});
            skLineSegment(sketch, "E194.3.2", {"start": v(20.47, -26.41) * mm, "end": v(20.47, -19.91) * mm});
            skLineSegment(sketch, "E194.3.3", {"start": v(20.47, -19.91) * mm, "end": v(13.97, -19.91) * mm});
            skLineSegment(sketch, "E195.1", {"start": v(-9.03, -19.91) * mm, "end": v(-9.03, -26.41) * mm});
            skLineSegment(sketch, "E195.2", {"start": v(-9.03, -19.91) * mm, "end": v(-15.53, -19.91) * mm});
            skLineSegment(sketch, "E195.3", {"start": v(-15.53, -19.91) * mm, "end": v(-15.53, -26.41) * mm});
            skLineSegment(sketch, "E196.0", {"start": v(-9.03, -26.41) * mm, "end": v(-15.53, -26.41) * mm});
            skLineSegment(sketch, "E197", {"start": v(-15.53, -19.91) * mm, "end": v(-9.03, -26.41) * mm, "construction": true});
            skLineSegment(sketch, "E198", {"start": v(-5.7, -19.91) * mm, "end": v(0.8, -26.41) * mm, "construction": true});
            skLineSegment(sketch, "E199", {"start": v(4.13, -19.91) * mm, "end": v(10.63, -26.41) * mm, "construction": true});
            skLineSegment(sketch, "E200", {"start": v(13.97, -19.91) * mm, "end": v(20.47, -26.41) * mm, "construction": true});
            skCircle(sketch, "E201", {"center": v(-12.28, -23.16) * mm, "radius": 1.9 * mm});
            skCircle(sketch, "E202", {"center": v(-2.45, -23.16) * mm, "radius": 1.9 * mm});
            skCircle(sketch, "E203", {"center": v(7.38, -23.16) * mm, "radius": 1.9 * mm});
            skCircle(sketch, "E204", {"center": v(17.22, -23.16) * mm, "radius": 1.9 * mm});
            skSolve(sketch);
        }
        {
            var Q0;
            Q0=makeQuery(id+"F12.imprint","IMPRINT",FACE,{"disambiguationData":[TD([[makeQuery(id+"F12.imprint","IMPRINT",EDGE,{"derivedFrom":sQuery(id+"F12.wireOp",EDGE,"E201")}),1.0]])]});
            var Q1;
            Q1=makeQuery(id+"F12.imprint","IMPRINT",FACE,{"disambiguationData":[TD([[makeQuery(id+"F12.imprint","IMPRINT",EDGE,{"derivedFrom":sQuery(id+"F12.wireOp",EDGE,"E202")}),1.0]])]});
            var Q2;
            Q2=makeQuery(id+"F12.imprint","IMPRINT",FACE,{"disambiguationData":[TD([[makeQuery(id+"F12.imprint","IMPRINT",EDGE,{"derivedFrom":sQuery(id+"F12.wireOp",EDGE,"E203")}),1.0]])]});
            var Q3;
            Q3=makeQuery(id+"F12.imprint","IMPRINT",FACE,{"disambiguationData":[TD([[makeQuery(id+"F12.imprint","IMPRINT",EDGE,{"derivedFrom":sQuery(id+"F12.wireOp",EDGE,"E204")}),1.0]])]});
            extrude(context, id + "F13", {"entities" : qUnion([Q0, Q1, Q2, Q3]), "depth" : 2.54 * mm, "offsetDistance" : 25.4 * mm});
        }
        {
            var Q0;
            Q0=makeQuery(id+"F1.opExtrude","CAP_FACE",FACE,{"disambiguationData":[OSD([sQuery(id+"F0.wireOp",EDGE,"E0.bottom"),sQuery(id+"F0.wireOp",EDGE,"E0.top"),sQuery(id+"F0.wireOp",EDGE,"E0.left"),sQuery(id+"F0.wireOp",EDGE,"E0.right"),sQuery(id+"F0.wireOp",EDGE,"E14"),sQuery(id+"F0.wireOp",EDGE,"E15"),sQuery(id+"F0.wireOp",EDGE,"E16"),sQuery(id+"F0.wireOp",EDGE,"E17")])],"isStart":false});
            var sketch = newSketch(context, id + "F14", { "sketchPlane" : qUnion([Q0])});
            skText(sketch, "E205", { "text": "KK2.1x FC", "fontName": "OpenSans-Bold.ttf"});
            skLineSegment(sketch, "E206.0", {"start": v(28.47, 22.59) * mm, "end": v(28.47, -29.41) * mm});
            skLineSegment(sketch, "E207.0", {"start": v(-23.53, 22.59) * mm, "end": v(-23.53, -29.41) * mm});
            skLineSegment(sketch, "E208.0", {"start": v(-15.53, 6.09) * mm, "end": v(20.47, 6.09) * mm});
            skLineSegment(sketch, "E209", {"start": v(-13.74, 15.98) * mm, "end": v(-13.74, 22.59) * mm, "construction": true});
            skLineSegment(sketch, "E210", {"start": v(-23.53, 22.59) * mm, "end": v(-13.74, 15.98) * mm, "construction": true});
            const initialGuessF14  = {"E205": [-0.02353, 0.0082, 1, 0, 0.00779]};
            skSetInitialGuess(sketch, initialGuessF14);
            skSolve(sketch);
        }
        {
            var Q0;
            Q0=makeQuery(id+"F14.imprint","IMPRINT",FACE,{"disambiguationData":[TD([[makeQuery(id+"F14.imprint","IMPRINT",EDGE,{"derivedFrom":sQuery(id+"F14.wireOp",EDGE,"E205.sketch_text.stroke-50")}),-1.0]])]});
            var Q1;
            Q1=makeQuery(id+"F14.imprint","IMPRINT",FACE,{"disambiguationData":[TD([[makeQuery(id+"F14.imprint","IMPRINT",EDGE,{"derivedFrom":sQuery(id+"F14.wireOp",EDGE,"E205.sketch_text.stroke-58")}),-1.0]])]});
            var Q2;
            Q2=makeQuery(id+"F14.imprint","IMPRINT",FACE,{"disambiguationData":[TD([[makeQuery(id+"F14.imprint","IMPRINT",EDGE,{"derivedFrom":sQuery(id+"F14.wireOp",EDGE,"E205.sketch_text.stroke-68")}),-1.0]])]});
            var Q3;
            Q3=makeQuery(id+"F14.imprint","IMPRINT",FACE,{"disambiguationData":[TD([[makeQuery(id+"F14.imprint","IMPRINT",EDGE,{"derivedFrom":sQuery(id+"F14.wireOp",EDGE,"E205.sketch_text.stroke-80")}),-1.0]])]});
            var Q4;
            Q4=makeQuery(id+"F14.imprint","IMPRINT",FACE,{"disambiguationData":[TD([[makeQuery(id+"F14.imprint","IMPRINT",EDGE,{"derivedFrom":sQuery(id+"F14.wireOp",EDGE,"E205.sketch_text.stroke-90")}),-1.0]])]});
            var Q5;
            Q5=makeQuery(id+"F14.imprint","IMPRINT",FACE,{"disambiguationData":[TD([[makeQuery(id+"F14.imprint","IMPRINT",EDGE,{"derivedFrom":sQuery(id+"F14.wireOp",EDGE,"E205.sketch_text.stroke-0")}),-1.0]])]});
            var Q6;
            Q6=makeQuery(id+"F14.imprint","IMPRINT",FACE,{"disambiguationData":[TD([[makeQuery(id+"F14.imprint","IMPRINT",EDGE,{"derivedFrom":sQuery(id+"F14.wireOp",EDGE,"E205.sketch_text.stroke-13")}),-1.0]])]});
            var Q7;
            Q7=makeQuery(id+"F14.imprint","IMPRINT",FACE,{"disambiguationData":[TD([[makeQuery(id+"F14.imprint","IMPRINT",EDGE,{"derivedFrom":sQuery(id+"F14.wireOp",EDGE,"E205.sketch_text.stroke-26")}),-1.0]])]});
            extrude(context, id + "F15", {"entities" : qUnion([Q0, Q1, Q2, Q3, Q4, Q5, Q6, Q7]), "depth" : 2.54 * mm, "offsetDistance" : 25.4 * mm});
        }
        {
            var Q0;
            Q0=makeQuery(id+"F5.opExtrude","CAP_FACE",FACE,{"disambiguationData":[OSD([sQuery(id+"F4.wireOp",EDGE,"E22.bottom"),sQuery(id+"F4.wireOp",EDGE,"E22.top"),sQuery(id+"F4.wireOp",EDGE,"E22.left"),sQuery(id+"F4.wireOp",EDGE,"E22.right")])],"isStart":false});
            var sketch = newSketch(context, id + "F16", { "sketchPlane" : qUnion([Q0])});
            skLineSegment(sketch, "E211.0", {"start": v(-23.53, 2.84) * mm, "end": v(-15.53, 2.84) * mm});
            skLineSegment(sketch, "E211.1", {"start": v(-23.53, 2.84) * mm, "end": v(-23.53, -11.66) * mm});
            skLineSegment(sketch, "E211.2", {"start": v(-23.53, -11.66) * mm, "end": v(-15.53, -11.66) * mm});
            skLineSegment(sketch, "E211.3", {"start": v(-15.53, 2.84) * mm, "end": v(-15.53, -11.66) * mm});
            skLineSegment(sketch, "E212.0", {"start": v(20.47, 5.09) * mm, "end": v(20.47, -18.41) * mm});
            skLineSegment(sketch, "E212.1", {"start": v(28.47, 5.09) * mm, "end": v(28.47, -18.41) * mm});
            skLineSegment(sketch, "E212.2", {"start": v(28.47, 5.09) * mm, "end": v(20.47, 5.09) * mm});
            skLineSegment(sketch, "E212.3", {"start": v(28.47, -18.41) * mm, "end": v(20.47, -18.41) * mm});
            skText(sketch, "E213", { "text": "AIL\n", "fontName": "OpenSans-Regular.ttf"});
            skText(sketch, "E214", { "text": "ELE", "fontName": "OpenSans-Regular.ttf"});
            skText(sketch, "E215", { "text": "THR", "fontName": "OpenSans-Regular.ttf"});
            skText(sketch, "E216", { "text": "RUD", "fontName": "OpenSans-Regular.ttf"});
            skText(sketch, "E217", { "text": "GEA", "fontName": "OpenSans-Regular.ttf"});
            skText(sketch, "E218", { "text": "LF", "fontName": "OpenSans-Regular.ttf"});
            skText(sketch, "E219", { "text": "RF\n", "fontName": "OpenSans-Regular.ttf"});
            skText(sketch, "E220", { "text": "RB", "fontName": "OpenSans-Regular.ttf"});
            skText(sketch, "E221", { "text": "LB\n", "fontName": "OpenSans-Regular.ttf"});
            skLineSegment(sketch, "E222.0", {"start": v(-23.53, -0.06) * mm, "end": v(-15.53, -0.06) * mm});
            skLineSegment(sketch, "E222.1", {"start": v(-23.53, -2.96) * mm, "end": v(-15.53, -2.96) * mm});
            skLineSegment(sketch, "E222.2", {"start": v(-23.53, -5.86) * mm, "end": v(-15.53, -5.86) * mm});
            skLineSegment(sketch, "E222.3", {"start": v(-23.53, -8.76) * mm, "end": v(-15.53, -8.76) * mm});
            skLineSegment(sketch, "E222.4", {"start": v(20.47, -15.48) * mm, "end": v(28.47, -15.48) * mm});
            skLineSegment(sketch, "E222.5", {"start": v(20.47, -12.54) * mm, "end": v(28.47, -12.54) * mm});
            skLineSegment(sketch, "E222.6", {"start": v(20.47, -9.6) * mm, "end": v(28.47, -9.6) * mm});
            skLineSegment(sketch, "E222.7", {"start": v(20.47, -6.66) * mm, "end": v(28.47, -6.66) * mm});
            skLineSegment(sketch, "E222.8", {"start": v(20.47, -3.73) * mm, "end": v(28.47, -3.73) * mm});
            skLineSegment(sketch, "E222.9", {"start": v(20.47, -0.79) * mm, "end": v(28.47, -0.79) * mm});
            skLineSegment(sketch, "E222.10", {"start": v(20.47, 2.15) * mm, "end": v(28.47, 2.15) * mm});
            skText(sketch, "E223", { "text": "PSH", "fontName": "OpenSans-Regular.ttf"});
            skText(sketch, "E224", { "text": "RUD\n", "fontName": "OpenSans-Regular.ttf"});
            skText(sketch, "E225", { "text": "ELE", "fontName": "OpenSans-Regular.ttf"});
            skText(sketch, "E226", { "text": "AIL", "fontName": "OpenSans-Regular.ttf"});
            skLineSegment(sketch, "E227", {"start": v(13.12, 5.09) * mm, "end": v(13.12, -16.16) * mm});
            skLineSegment(sketch, "E228", {"start": v(15.5, 2.51) * mm, "end": v(15.5, 1.85) * mm});
            skLineSegment(sketch, "E229", {"start": v(15.65, -0.06) * mm, "end": v(15.65, -0.72) * mm});
            skLineSegment(sketch, "E230", {"start": v(16.02, -2.64) * mm, "end": v(16.02, -3.3) * mm});
            skLineSegment(sketch, "E231", {"start": v(15.97, -5.2) * mm, "end": v(15.97, -5.87) * mm});
            skLineSegment(sketch, "E232", {"start": v(16.2, -7.78) * mm, "end": v(16.2, -8.44) * mm});
            skLineSegment(sketch, "E233", {"start": v(16.3, -10.36) * mm, "end": v(16.3, -11.02) * mm});
            skLineSegment(sketch, "E234", {"start": v(16.1, -12.93) * mm, "end": v(16.1, -13.6) * mm});
            skLineSegment(sketch, "E235", {"start": v(15.4, 5.09) * mm, "end": v(15.4, 4.43) * mm});
            skLineSegment(sketch, "E236", {"start": v(15.47, -15.5) * mm, "end": v(15.47, -16.16) * mm});
            skLineSegment(sketch, "E237", {"start": v(-10.9, 5.09) * mm, "end": v(-10.9, -16.16) * mm});
            skLineSegment(sketch, "E238", {"start": v(-23.53, -5.86) * mm, "end": v(-10.9, -5.86) * mm, "construction": true});
            skLineSegment(sketch, "E239", {"start": v(-23.53, -8.76) * mm, "end": v(-10.9, -8.76) * mm, "construction": true});
            skLineSegment(sketch, "E240", {"start": v(-23.53, -11.66) * mm, "end": v(-10.9, -11.66) * mm, "construction": true});
            skLineSegment(sketch, "E241", {"start": v(-23.53, -0.06) * mm, "end": v(-10.9, -0.06) * mm, "construction": true});
            skLineSegment(sketch, "E242", {"start": v(-23.53, 2.84) * mm, "end": v(-10.9, 2.84) * mm, "construction": true});
            skLineSegment(sketch, "E243", {"start": v(-23.53, -2.96) * mm, "end": v(-10.9, -2.96) * mm, "construction": true});
            skLineSegment(sketch, "E244.0", {"start": v(-21.72, -2.07) * mm, "end": v(-22.72, -2.07) * mm});
            skLineSegment(sketch, "E244.1", {"start": v(-16.34, -2.07) * mm, "end": v(-17.34, -2.07) * mm});
            skLineSegment(sketch, "E244.2", {"start": v(-16.34, -0.96) * mm, "end": v(-17.34, -0.96) * mm});
            skLineSegment(sketch, "E244.3", {"start": v(-21.72, -0.96) * mm, "end": v(-22.72, -0.96) * mm});
            skLineSegment(sketch, "E244.4", {"start": v(-21.72, 0.83) * mm, "end": v(-22.72, 0.83) * mm});
            skLineSegment(sketch, "E244.5", {"start": v(-21.72, 1.94) * mm, "end": v(-22.72, 1.94) * mm});
            skLineSegment(sketch, "E244.6", {"start": v(-20.1, 1.94) * mm, "end": v(-19.1, 1.94) * mm});
            skLineSegment(sketch, "E244.7", {"start": v(-16.34, 0.83) * mm, "end": v(-17.34, 0.83) * mm});
            skLineSegment(sketch, "E244.8", {"start": v(-21.72, -3.86) * mm, "end": v(-22.72, -3.86) * mm});
            skLineSegment(sketch, "E244.9", {"start": v(-21.72, -4.97) * mm, "end": v(-22.72, -4.97) * mm});
            skLineSegment(sketch, "E244.10", {"start": v(-16.34, -3.86) * mm, "end": v(-17.34, -3.86) * mm});
            skLineSegment(sketch, "E244.11", {"start": v(-16.34, -4.97) * mm, "end": v(-17.34, -4.97) * mm});
            skLineSegment(sketch, "E244.12", {"start": v(-16.34, -6.76) * mm, "end": v(-17.34, -6.76) * mm});
            skLineSegment(sketch, "E244.13", {"start": v(-16.34, -7.87) * mm, "end": v(-17.34, -7.87) * mm});
            skLineSegment(sketch, "E244.14", {"start": v(-20.1, -7.87) * mm, "end": v(-19.1, -7.87) * mm});
            skLineSegment(sketch, "E244.15", {"start": v(-21.72, -6.76) * mm, "end": v(-22.72, -6.76) * mm});
            skLineSegment(sketch, "E244.16", {"start": v(-21.72, -9.66) * mm, "end": v(-22.72, -9.66) * mm});
            skLineSegment(sketch, "E244.17", {"start": v(-20.1, -10.77) * mm, "end": v(-19.1, -10.77) * mm});
            skLineSegment(sketch, "E244.18", {"start": v(-16.34, -9.66) * mm, "end": v(-17.34, -9.66) * mm});
            skLineSegment(sketch, "E244.19", {"start": v(-16.34, -10.77) * mm, "end": v(-17.34, -10.77) * mm});
            skLineSegment(sketch, "E245", {"start": v(-22.72, 1.94) * mm, "end": v(-10.9, 1.94) * mm, "construction": true});
            skLineSegment(sketch, "E246", {"start": v(-22.72, 0.83) * mm, "end": v(-10.9, 0.83) * mm, "construction": true});
            skLineSegment(sketch, "E247", {"start": v(-22.72, -2.07) * mm, "end": v(-10.9, -2.07) * mm, "construction": true});
            skLineSegment(sketch, "E248", {"start": v(-22.72, -0.96) * mm, "end": v(-10.9, -0.96) * mm, "construction": true});
            skLineSegment(sketch, "E249", {"start": v(-22.72, -3.86) * mm, "end": v(-10.9, -3.86) * mm, "construction": true});
            skLineSegment(sketch, "E250", {"start": v(-22.72, -4.97) * mm, "end": v(-10.9, -4.97) * mm, "construction": true});
            skLineSegment(sketch, "E251", {"start": v(-22.72, -9.66) * mm, "end": v(-10.9, -9.66) * mm, "construction": true});
            skLineSegment(sketch, "E252", {"start": v(-20.1, -10.77) * mm, "end": v(-10.9, -10.77) * mm, "construction": true});
            skLineSegment(sketch, "E253", {"start": v(-22.72, -6.76) * mm, "end": v(-10.9, -6.76) * mm, "construction": true});
            skLineSegment(sketch, "E254", {"start": v(-20.1, -7.87) * mm, "end": v(-10.9, -7.87) * mm, "construction": true});
            skText(sketch, "E255", { "text": "OUT1\n", "fontName": "OpenSans-Regular.ttf"});
            skText(sketch, "E256", { "text": "OUT2\n", "fontName": "OpenSans-Regular.ttf"});
            skText(sketch, "E257", { "text": "OUT3\n", "fontName": "OpenSans-Regular.ttf"});
            skText(sketch, "E258", { "text": "OUT4\n", "fontName": "OpenSans-Regular.ttf"});
            skText(sketch, "E259", { "text": "OUT5\n", "fontName": "OpenSans-Regular.ttf"});
            skText(sketch, "E260", { "text": "OUT6\n", "fontName": "OpenSans-Regular.ttf"});
            skText(sketch, "E261", { "text": "OUT7\n", "fontName": "OpenSans-Regular.ttf"});
            skText(sketch, "E262", { "text": "OUT8", "fontName": "OpenSans-Regular.ttf"});
            const initialGuessF16  = {"E213": [-0.01317, 0.00083, 1, 0, 0.0011], "E214": [-0.01342, -0.00207, 1, 0, 0.0011], "E215": [-0.0141, -0.00504, 1, 0, 0.00118], "E216": [-0.0141, -0.00787, 1, 0, 0.0011], "E217": [-0.01395, -0.01077, 1, 0, 0.0011], "E218": [0.01312, 0.00251, 1, 0, 0.00191], "E219": [0.01312, -6e-05, 1, 0, 0.00191], "E220": [0.01312, -0.00264, 1, 0, 0.00191], "E221": [0.01312, -0.0052, 1, 0, 0.00191], "E223": [0.01312, -0.00778, 1, 0, 0.00191], "E224": [0.01312, -0.01036, 1, 0, 0.00191], "E225": [0.01312, -0.01293, 1, 0, 0.00191], "E226": [0.01312, -0.0155, 1, 0, 0.00191], "E255": [0.00654, 0.00251, 1, 0, 0.00191], "E256": [0.00609, -6e-05, 1, 0, 0.00191], "E257": [0.0061, -0.00264, 1, 0, 0.00191], "E258": [0.006, -0.0052, 1, 0, 0.00191], "E259": [0.0061, -0.00778, 1, 0, 0.00191], "E260": [0.00607, -0.01036, 1, 0, 0.00191], "E261": [0.00608, -0.01293, 1, 0, 0.00191], "E262": [0.00608, -0.0155, 1, 0, 0.00191]};
            skSetInitialGuess(sketch, initialGuessF16);
            skSolve(sketch);
        }
        {
            var Q0;
            Q0=makeQuery(id+"F16.imprint","IMPRINT",FACE,{"disambiguationData":[TD([[makeQuery(id+"F16.imprint","IMPRINT",EDGE,{"derivedFrom":sQuery(id+"F16.wireOp",EDGE,"E213.sketch_text.stroke-0")}),-1.0]])]});
            var Q1;
            Q1=makeQuery(id+"F16.imprint","IMPRINT",FACE,{"disambiguationData":[TD([[makeQuery(id+"F16.imprint","IMPRINT",EDGE,{"derivedFrom":sQuery(id+"F16.wireOp",EDGE,"E213.sketch_text.stroke-13")}),-1.0]])]});
            var Q2;
            Q2=makeQuery(id+"F16.imprint","IMPRINT",FACE,{"disambiguationData":[TD([[makeQuery(id+"F16.imprint","IMPRINT",EDGE,{"derivedFrom":sQuery(id+"F16.wireOp",EDGE,"E213.sketch_text.stroke-17")}),-1.0]])]});
            var Q3;
            Q3=makeQuery(id+"F16.imprint","IMPRINT",FACE,{"disambiguationData":[TD([[makeQuery(id+"F16.imprint","IMPRINT",EDGE,{"derivedFrom":sQuery(id+"F16.wireOp",EDGE,"E214.sketch_text.stroke-0")}),-1.0]])]});
            var Q4;
            Q4=makeQuery(id+"F16.imprint","IMPRINT",FACE,{"disambiguationData":[TD([[makeQuery(id+"F16.imprint","IMPRINT",EDGE,{"derivedFrom":sQuery(id+"F16.wireOp",EDGE,"E214.sketch_text.stroke-12")}),-1.0]])]});
            var Q5;
            Q5=makeQuery(id+"F16.imprint","IMPRINT",FACE,{"disambiguationData":[TD([[makeQuery(id+"F16.imprint","IMPRINT",EDGE,{"derivedFrom":sQuery(id+"F16.wireOp",EDGE,"E214.sketch_text.stroke-18")}),-1.0]])]});
            var Q6;
            Q6=makeQuery(id+"F16.imprint","IMPRINT",FACE,{"disambiguationData":[TD([[makeQuery(id+"F16.imprint","IMPRINT",EDGE,{"derivedFrom":sQuery(id+"F16.wireOp",EDGE,"E215.sketch_text.stroke-0")}),-1.0]])]});
            var Q7;
            Q7=makeQuery(id+"F16.imprint","IMPRINT",FACE,{"disambiguationData":[TD([[makeQuery(id+"F16.imprint","IMPRINT",EDGE,{"derivedFrom":sQuery(id+"F16.wireOp",EDGE,"E215.sketch_text.stroke-8")}),-1.0]])]});
            var Q8;
            Q8=makeQuery(id+"F16.imprint","IMPRINT",FACE,{"disambiguationData":[TD([[makeQuery(id+"F16.imprint","IMPRINT",EDGE,{"derivedFrom":sQuery(id+"F16.wireOp",EDGE,"E215.sketch_text.stroke-20")}),-1.0]])]});
            var Q9;
            Q9=makeQuery(id+"F16.imprint","IMPRINT",FACE,{"disambiguationData":[TD([[makeQuery(id+"F16.imprint","IMPRINT",EDGE,{"derivedFrom":sQuery(id+"F16.wireOp",EDGE,"E216.sketch_text.stroke-0")}),-1.0]])]});
            var Q10;
            Q10=makeQuery(id+"F16.imprint","IMPRINT",FACE,{"disambiguationData":[TD([[makeQuery(id+"F16.imprint","IMPRINT",EDGE,{"derivedFrom":sQuery(id+"F16.wireOp",EDGE,"E216.sketch_text.stroke-18")}),-1.0]])]});
            var Q11;
            Q11=makeQuery(id+"F16.imprint","IMPRINT",FACE,{"disambiguationData":[TD([[makeQuery(id+"F16.imprint","IMPRINT",EDGE,{"derivedFrom":sQuery(id+"F16.wireOp",EDGE,"E216.sketch_text.stroke-32")}),-1.0]])]});
            var Q12;
            Q12=makeQuery(id+"F16.imprint","IMPRINT",FACE,{"disambiguationData":[TD([[makeQuery(id+"F16.imprint","IMPRINT",EDGE,{"derivedFrom":sQuery(id+"F16.wireOp",EDGE,"E217.sketch_text.stroke-0")}),-1.0]])]});
            var Q13;
            Q13=makeQuery(id+"F16.imprint","IMPRINT",FACE,{"disambiguationData":[TD([[makeQuery(id+"F16.imprint","IMPRINT",EDGE,{"derivedFrom":sQuery(id+"F16.wireOp",EDGE,"E217.sketch_text.stroke-20")}),-1.0]])]});
            var Q14;
            Q14=makeQuery(id+"F16.imprint","IMPRINT",FACE,{"disambiguationData":[TD([[makeQuery(id+"F16.imprint","IMPRINT",EDGE,{"derivedFrom":sQuery(id+"F16.wireOp",EDGE,"E217.sketch_text.stroke-32")}),-1.0]])]});
            extrude(context, id + "F17", {"entities" : qUnion([Q0, Q1, Q2, Q3, Q4, Q5, Q6, Q7, Q8, Q9, Q10, Q11, Q12, Q13, Q14]), "depth" : 0.25 * mm, "offsetDistance" : 25.4 * mm});
        }
        {
            var Q0;
            Q0=makeQuery(id+"F16.imprint","IMPRINT",FACE,{"disambiguationData":[TD([[makeQuery(id+"F16.imprint","IMPRINT",EDGE,{"derivedFrom":sQuery(id+"F16.wireOp",EDGE,"E255.sketch_text.stroke-0")}),-1.0]])]});
            var Q1;
            Q1=makeQuery(id+"F16.imprint","IMPRINT",FACE,{"disambiguationData":[TD([[makeQuery(id+"F16.imprint","IMPRINT",EDGE,{"derivedFrom":sQuery(id+"F16.wireOp",EDGE,"E255.sketch_text.stroke-16")}),-1.0]])]});
            var Q2;
            Q2=makeQuery(id+"F16.imprint","IMPRINT",FACE,{"disambiguationData":[TD([[makeQuery(id+"F16.imprint","IMPRINT",EDGE,{"derivedFrom":sQuery(id+"F16.wireOp",EDGE,"E255.sketch_text.stroke-30")}),-1.0]])]});
            var Q3;
            Q3=makeQuery(id+"F16.imprint","IMPRINT",FACE,{"disambiguationData":[TD([[makeQuery(id+"F16.imprint","IMPRINT",EDGE,{"derivedFrom":sQuery(id+"F16.wireOp",EDGE,"E255.sketch_text.stroke-38")}),-1.0]])]});
            var Q4;
            Q4=makeQuery(id+"F16.imprint","IMPRINT",FACE,{"disambiguationData":[TD([[makeQuery(id+"F16.imprint","IMPRINT",EDGE,{"derivedFrom":sQuery(id+"F16.wireOp",EDGE,"E218.sketch_text.stroke-0")}),-1.0]])]});
            var Q5;
            Q5=makeQuery(id+"F16.imprint","IMPRINT",FACE,{"disambiguationData":[TD([[makeQuery(id+"F16.imprint","IMPRINT",EDGE,{"derivedFrom":sQuery(id+"F16.wireOp",EDGE,"E218.sketch_text.stroke-6")}),-1.0]])]});
            var Q6;
            Q6=makeQuery(id+"F16.imprint","IMPRINT",FACE,{"disambiguationData":[TD([[makeQuery(id+"F16.imprint","IMPRINT",EDGE,{"derivedFrom":sQuery(id+"F16.wireOp",EDGE,"E256.sketch_text.stroke-0")}),-1.0]])]});
            var Q7;
            Q7=makeQuery(id+"F16.imprint","IMPRINT",FACE,{"disambiguationData":[TD([[makeQuery(id+"F16.imprint","IMPRINT",EDGE,{"derivedFrom":sQuery(id+"F16.wireOp",EDGE,"E256.sketch_text.stroke-16")}),-1.0]])]});
            var Q8;
            Q8=makeQuery(id+"F16.imprint","IMPRINT",FACE,{"disambiguationData":[TD([[makeQuery(id+"F16.imprint","IMPRINT",EDGE,{"derivedFrom":sQuery(id+"F16.wireOp",EDGE,"E256.sketch_text.stroke-30")}),-1.0]])]});
            var Q9;
            Q9=makeQuery(id+"F16.imprint","IMPRINT",FACE,{"disambiguationData":[TD([[makeQuery(id+"F16.imprint","IMPRINT",EDGE,{"derivedFrom":sQuery(id+"F16.wireOp",EDGE,"E256.sketch_text.stroke-38")}),-1.0]])]});
            var Q10;
            Q10=makeQuery(id+"F16.imprint","IMPRINT",FACE,{"disambiguationData":[TD([[makeQuery(id+"F16.imprint","IMPRINT",EDGE,{"derivedFrom":sQuery(id+"F16.wireOp",EDGE,"E219.sketch_text.stroke-0")}),-1.0]])]});
            var Q11;
            Q11=makeQuery(id+"F16.imprint","IMPRINT",FACE,{"disambiguationData":[TD([[makeQuery(id+"F16.imprint","IMPRINT",EDGE,{"derivedFrom":sQuery(id+"F16.wireOp",EDGE,"E219.sketch_text.stroke-18")}),-1.0]])]});
            var Q12;
            Q12=makeQuery(id+"F16.imprint","IMPRINT",FACE,{"disambiguationData":[TD([[makeQuery(id+"F16.imprint","IMPRINT",EDGE,{"derivedFrom":sQuery(id+"F16.wireOp",EDGE,"E257.sketch_text.stroke-0")}),-1.0]])]});
            var Q13;
            Q13=makeQuery(id+"F16.imprint","IMPRINT",FACE,{"disambiguationData":[TD([[makeQuery(id+"F16.imprint","IMPRINT",EDGE,{"derivedFrom":sQuery(id+"F16.wireOp",EDGE,"E257.sketch_text.stroke-16")}),-1.0]])]});
            var Q14;
            Q14=makeQuery(id+"F16.imprint","IMPRINT",FACE,{"disambiguationData":[TD([[makeQuery(id+"F16.imprint","IMPRINT",EDGE,{"derivedFrom":sQuery(id+"F16.wireOp",EDGE,"E257.sketch_text.stroke-30")}),-1.0]])]});
            var Q15;
            Q15=makeQuery(id+"F16.imprint","IMPRINT",FACE,{"disambiguationData":[TD([[makeQuery(id+"F16.imprint","IMPRINT",EDGE,{"derivedFrom":sQuery(id+"F16.wireOp",EDGE,"E257.sketch_text.stroke-38")}),-1.0]])]});
            var Q16;
            Q16=makeQuery(id+"F16.imprint","IMPRINT",FACE,{"disambiguationData":[TD([[makeQuery(id+"F16.imprint","IMPRINT",EDGE,{"derivedFrom":sQuery(id+"F16.wireOp",EDGE,"E220.sketch_text.stroke-0")}),-1.0]])]});
            var Q17;
            Q17=makeQuery(id+"F16.imprint","IMPRINT",FACE,{"disambiguationData":[TD([[makeQuery(id+"F16.imprint","IMPRINT",EDGE,{"derivedFrom":sQuery(id+"F16.wireOp",EDGE,"E220.sketch_text.stroke-18")}),-1.0]])]});
            var Q18;
            Q18=makeQuery(id+"F16.imprint","IMPRINT",FACE,{"disambiguationData":[TD([[makeQuery(id+"F16.imprint","IMPRINT",EDGE,{"derivedFrom":sQuery(id+"F16.wireOp",EDGE,"E258.sketch_text.stroke-0")}),-1.0]])]});
            var Q19;
            Q19=makeQuery(id+"F16.imprint","IMPRINT",FACE,{"disambiguationData":[TD([[makeQuery(id+"F16.imprint","IMPRINT",EDGE,{"derivedFrom":sQuery(id+"F16.wireOp",EDGE,"E258.sketch_text.stroke-16")}),-1.0]])]});
            var Q20;
            Q20=makeQuery(id+"F16.imprint","IMPRINT",FACE,{"disambiguationData":[TD([[makeQuery(id+"F16.imprint","IMPRINT",EDGE,{"derivedFrom":sQuery(id+"F16.wireOp",EDGE,"E258.sketch_text.stroke-30")}),-1.0]])]});
            var Q21;
            Q21=makeQuery(id+"F16.imprint","IMPRINT",FACE,{"disambiguationData":[TD([[makeQuery(id+"F16.imprint","IMPRINT",EDGE,{"derivedFrom":sQuery(id+"F16.wireOp",EDGE,"E258.sketch_text.stroke-38")}),-1.0]])]});
            var Q22;
            Q22=makeQuery(id+"F16.imprint","IMPRINT",FACE,{"disambiguationData":[TD([[makeQuery(id+"F16.imprint","IMPRINT",EDGE,{"derivedFrom":sQuery(id+"F16.wireOp",EDGE,"E221.sketch_text.stroke-0")}),-1.0]])]});
            var Q23;
            Q23=makeQuery(id+"F16.imprint","IMPRINT",FACE,{"disambiguationData":[TD([[makeQuery(id+"F16.imprint","IMPRINT",EDGE,{"derivedFrom":sQuery(id+"F16.wireOp",EDGE,"E221.sketch_text.stroke-6")}),-1.0]])]});
            var Q24;
            Q24=makeQuery(id+"F16.imprint","IMPRINT",FACE,{"disambiguationData":[TD([[makeQuery(id+"F16.imprint","IMPRINT",EDGE,{"derivedFrom":sQuery(id+"F16.wireOp",EDGE,"E259.sketch_text.stroke-0")}),-1.0]])]});
            var Q25;
            Q25=makeQuery(id+"F16.imprint","IMPRINT",FACE,{"disambiguationData":[TD([[makeQuery(id+"F16.imprint","IMPRINT",EDGE,{"derivedFrom":sQuery(id+"F16.wireOp",EDGE,"E259.sketch_text.stroke-16")}),-1.0]])]});
            var Q26;
            Q26=makeQuery(id+"F16.imprint","IMPRINT",FACE,{"disambiguationData":[TD([[makeQuery(id+"F16.imprint","IMPRINT",EDGE,{"derivedFrom":sQuery(id+"F16.wireOp",EDGE,"E259.sketch_text.stroke-30")}),-1.0]])]});
            var Q27;
            Q27=makeQuery(id+"F16.imprint","IMPRINT",FACE,{"disambiguationData":[TD([[makeQuery(id+"F16.imprint","IMPRINT",EDGE,{"derivedFrom":sQuery(id+"F16.wireOp",EDGE,"E259.sketch_text.stroke-38")}),-1.0]])]});
            var Q28;
            Q28=makeQuery(id+"F16.imprint","IMPRINT",FACE,{"disambiguationData":[TD([[makeQuery(id+"F16.imprint","IMPRINT",EDGE,{"derivedFrom":sQuery(id+"F16.wireOp",EDGE,"E223.sketch_text.stroke-0")}),-1.0]])]});
            var Q29;
            Q29=makeQuery(id+"F16.imprint","IMPRINT",FACE,{"disambiguationData":[TD([[makeQuery(id+"F16.imprint","IMPRINT",EDGE,{"derivedFrom":sQuery(id+"F16.wireOp",EDGE,"E223.sketch_text.stroke-15")}),-1.0]])]});
            var Q30;
            Q30=makeQuery(id+"F16.imprint","IMPRINT",FACE,{"disambiguationData":[TD([[makeQuery(id+"F16.imprint","IMPRINT",EDGE,{"derivedFrom":sQuery(id+"F16.wireOp",EDGE,"E260.sketch_text.stroke-0")}),-1.0]])]});
            var Q31;
            Q31=makeQuery(id+"F16.imprint","IMPRINT",FACE,{"disambiguationData":[TD([[makeQuery(id+"F16.imprint","IMPRINT",EDGE,{"derivedFrom":sQuery(id+"F16.wireOp",EDGE,"E260.sketch_text.stroke-16")}),-1.0]])]});
            var Q32;
            Q32=makeQuery(id+"F16.imprint","IMPRINT",FACE,{"disambiguationData":[TD([[makeQuery(id+"F16.imprint","IMPRINT",EDGE,{"derivedFrom":sQuery(id+"F16.wireOp",EDGE,"E260.sketch_text.stroke-30")}),-1.0]])]});
            var Q33;
            Q33=makeQuery(id+"F16.imprint","IMPRINT",FACE,{"disambiguationData":[TD([[makeQuery(id+"F16.imprint","IMPRINT",EDGE,{"derivedFrom":sQuery(id+"F16.wireOp",EDGE,"E260.sketch_text.stroke-38")}),-1.0]])]});
            var Q34;
            Q34=makeQuery(id+"F16.imprint","IMPRINT",FACE,{"disambiguationData":[TD([[makeQuery(id+"F16.imprint","IMPRINT",EDGE,{"derivedFrom":sQuery(id+"F16.wireOp",EDGE,"E224.sketch_text.stroke-0")}),-1.0]])]});
            var Q35;
            Q35=makeQuery(id+"F16.imprint","IMPRINT",FACE,{"disambiguationData":[TD([[makeQuery(id+"F16.imprint","IMPRINT",EDGE,{"derivedFrom":sQuery(id+"F16.wireOp",EDGE,"E224.sketch_text.stroke-18")}),-1.0]])]});
            var Q36;
            Q36=makeQuery(id+"F16.imprint","IMPRINT",FACE,{"disambiguationData":[TD([[makeQuery(id+"F16.imprint","IMPRINT",EDGE,{"derivedFrom":sQuery(id+"F16.wireOp",EDGE,"E224.sketch_text.stroke-32")}),-1.0]])]});
            var Q37;
            Q37=makeQuery(id+"F16.imprint","IMPRINT",FACE,{"disambiguationData":[TD([[makeQuery(id+"F16.imprint","IMPRINT",EDGE,{"derivedFrom":sQuery(id+"F16.wireOp",EDGE,"E223.sketch_text.stroke-40")}),-1.0]])]});
            var Q38;
            Q38=makeQuery(id+"F16.imprint","IMPRINT",FACE,{"disambiguationData":[TD([[makeQuery(id+"F16.imprint","IMPRINT",EDGE,{"derivedFrom":sQuery(id+"F16.wireOp",EDGE,"E261.sketch_text.stroke-0")}),-1.0]])]});
            var Q39;
            Q39=makeQuery(id+"F16.imprint","IMPRINT",FACE,{"disambiguationData":[TD([[makeQuery(id+"F16.imprint","IMPRINT",EDGE,{"derivedFrom":sQuery(id+"F16.wireOp",EDGE,"E261.sketch_text.stroke-16")}),-1.0]])]});
            var Q40;
            Q40=makeQuery(id+"F16.imprint","IMPRINT",FACE,{"disambiguationData":[TD([[makeQuery(id+"F16.imprint","IMPRINT",EDGE,{"derivedFrom":sQuery(id+"F16.wireOp",EDGE,"E261.sketch_text.stroke-30")}),-1.0]])]});
            var Q41;
            Q41=makeQuery(id+"F16.imprint","IMPRINT",FACE,{"disambiguationData":[TD([[makeQuery(id+"F16.imprint","IMPRINT",EDGE,{"derivedFrom":sQuery(id+"F16.wireOp",EDGE,"E261.sketch_text.stroke-38")}),-1.0]])]});
            var Q42;
            Q42=makeQuery(id+"F16.imprint","IMPRINT",FACE,{"disambiguationData":[TD([[makeQuery(id+"F16.imprint","IMPRINT",EDGE,{"derivedFrom":sQuery(id+"F16.wireOp",EDGE,"E225.sketch_text.stroke-0")}),-1.0]])]});
            var Q43;
            Q43=makeQuery(id+"F16.imprint","IMPRINT",FACE,{"disambiguationData":[TD([[makeQuery(id+"F16.imprint","IMPRINT",EDGE,{"derivedFrom":sQuery(id+"F16.wireOp",EDGE,"E225.sketch_text.stroke-12")}),-1.0]])]});
            var Q44;
            Q44=makeQuery(id+"F16.imprint","IMPRINT",FACE,{"disambiguationData":[TD([[makeQuery(id+"F16.imprint","IMPRINT",EDGE,{"derivedFrom":sQuery(id+"F16.wireOp",EDGE,"E225.sketch_text.stroke-18")}),-1.0]])]});
            var Q45;
            Q45=makeQuery(id+"F16.imprint","IMPRINT",FACE,{"disambiguationData":[TD([[makeQuery(id+"F16.imprint","IMPRINT",EDGE,{"derivedFrom":sQuery(id+"F16.wireOp",EDGE,"E262.sketch_text.stroke-0")}),-1.0]])]});
            var Q46;
            Q46=makeQuery(id+"F16.imprint","IMPRINT",FACE,{"disambiguationData":[TD([[makeQuery(id+"F16.imprint","IMPRINT",EDGE,{"derivedFrom":sQuery(id+"F16.wireOp",EDGE,"E262.sketch_text.stroke-16")}),-1.0]])]});
            var Q47;
            Q47=makeQuery(id+"F16.imprint","IMPRINT",FACE,{"disambiguationData":[TD([[makeQuery(id+"F16.imprint","IMPRINT",EDGE,{"derivedFrom":sQuery(id+"F16.wireOp",EDGE,"E262.sketch_text.stroke-30")}),-1.0]])]});
            var Q48;
            Q48=makeQuery(id+"F16.imprint","IMPRINT",FACE,{"disambiguationData":[TD([[makeQuery(id+"F16.imprint","IMPRINT",EDGE,{"derivedFrom":sQuery(id+"F16.wireOp",EDGE,"E262.sketch_text.stroke-38")}),-1.0]])]});
            var Q49;
            Q49=makeQuery(id+"F16.imprint","IMPRINT",FACE,{"disambiguationData":[TD([[makeQuery(id+"F16.imprint","IMPRINT",EDGE,{"derivedFrom":sQuery(id+"F16.wireOp",EDGE,"E226.sketch_text.stroke-0")}),-1.0]])]});
            var Q50;
            Q50=makeQuery(id+"F16.imprint","IMPRINT",FACE,{"disambiguationData":[TD([[makeQuery(id+"F16.imprint","IMPRINT",EDGE,{"derivedFrom":sQuery(id+"F16.wireOp",EDGE,"E226.sketch_text.stroke-13")}),-1.0]])]});
            var Q51;
            Q51=makeQuery(id+"F16.imprint","IMPRINT",FACE,{"disambiguationData":[TD([[makeQuery(id+"F16.imprint","IMPRINT",EDGE,{"derivedFrom":sQuery(id+"F16.wireOp",EDGE,"E226.sketch_text.stroke-17")}),-1.0]])]});
            extrude(context, id + "F18", {"entities" : qUnion([Q0, Q1, Q2, Q3, Q4, Q5, Q6, Q7, Q8, Q9, Q10, Q11, Q12, Q13, Q14, Q15, Q16, Q17, Q18, Q19, Q20, Q21, Q22, Q23, Q24, Q25, Q26, Q27, Q28, Q29, Q30, Q31, Q32, Q33, Q34, Q35, Q36, Q37, Q38, Q39, Q40, Q41, Q42, Q43, Q44, Q45, Q46, Q47, Q48, Q49, Q50, Q51]), "depth" : 0.25 * mm, "offsetDistance" : 25.4 * mm});
        }
    });
